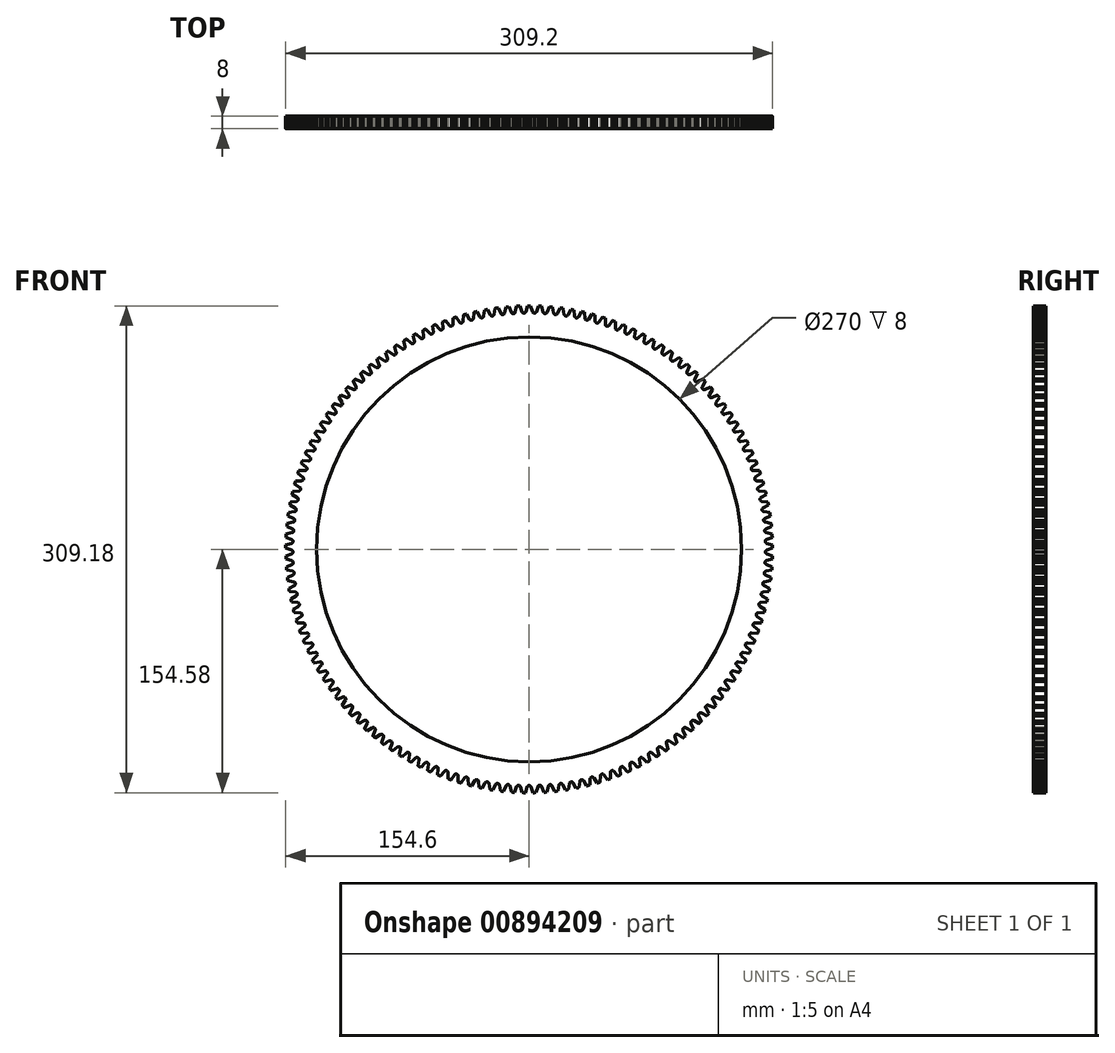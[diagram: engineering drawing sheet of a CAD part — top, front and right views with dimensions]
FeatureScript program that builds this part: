
annotation { "Feature Type Name" : "Feature", "Feature Type Description" : "" }
export const myFeature = defineFeature(function(context is Context, id is Id, definition is map)
    precondition{}
    {
        {
            var Q0;
            Q0=qCreatedBy(makeId("Front.planeOp"),FACE);
            var sketch = newSketch(context, id + "F0", { "sketchPlane" : qUnion([Q0])});
            skCircle(sketch, "E0", {"center": v(0, 0) * mm, "radius": 135 * mm});
            skArc(sketch, "E1", {"start": v(1, 154.6) * mm, "mid": v(0, 154.6) * mm, "end": v(-1, 154.6) * mm});
            skArc(sketch, "E2", {"start": v(2.15, 150.9) * mm, "mid": v(2.6, 150.27) * mm, "end": v(3.34, 150.03) * mm});
            skLineSegment(sketch, "E3", {"start": v(1, 154.6) * mm, "end": v(2.15, 150.9) * mm});
            skArc(sketch, "E4", {"start": v(-3.34, 150.03) * mm, "mid": v(-2.6, 150.27) * mm, "end": v(-2.15, 150.9) * mm});
            skLineSegment(sketch, "E5", {"start": v(-1, 154.6) * mm, "end": v(-2.15, 150.9) * mm});
            skArc(sketch, "E6", {"start": v(-5.89, 154.49) * mm, "mid": v(-6.89, 154.45) * mm, "end": v(-7.89, 154.4) * mm});
            skArc(sketch, "E7", {"start": v(-4.57, 150.85) * mm, "mid": v(-4.1, 150.24) * mm, "end": v(-3.34, 150.03) * mm});
            skLineSegment(sketch, "E8", {"start": v(-5.89, 154.49) * mm, "end": v(-4.57, 150.85) * mm});
            skArc(sketch, "E9", {"start": v(-10.02, 149.73) * mm, "mid": v(-9.3, 150) * mm, "end": v(-8.87, 150.66) * mm});
            skLineSegment(sketch, "E10", {"start": v(-7.89, 154.4) * mm, "end": v(-8.87, 150.66) * mm});
            skArc(sketch, "E11", {"start": v(-12.76, 154.07) * mm, "mid": v(-13.76, 153.99) * mm, "end": v(-14.76, 153.9) * mm});
            skArc(sketch, "E12", {"start": v(-11.3, 150.5) * mm, "mid": v(-10.78, 149.9) * mm, "end": v(-10.02, 149.73) * mm});
            skLineSegment(sketch, "E13", {"start": v(-12.76, 154.07) * mm, "end": v(-11.3, 150.5) * mm});
            skArc(sketch, "E14", {"start": v(-16.68, 149.13) * mm, "mid": v(-15.97, 149.44) * mm, "end": v(-15.57, 150.11) * mm});
            skLineSegment(sketch, "E15", {"start": v(-14.76, 153.9) * mm, "end": v(-15.57, 150.11) * mm});
            skArc(sketch, "E16", {"start": v(-19.61, 153.35) * mm, "mid": v(-20.6, 153.22) * mm, "end": v(-21.6, 153.08) * mm});
            skArc(sketch, "E17", {"start": v(-17.98, 149.84) * mm, "mid": v(-17.45, 149.27) * mm, "end": v(-16.68, 149.13) * mm});
            skLineSegment(sketch, "E18", {"start": v(-19.61, 153.35) * mm, "end": v(-17.98, 149.84) * mm});
            skArc(sketch, "E19", {"start": v(-23.3, 148.24) * mm, "mid": v(-22.6, 148.58) * mm, "end": v(-22.24, 149.27) * mm});
            skLineSegment(sketch, "E20", {"start": v(-21.6, 153.08) * mm, "end": v(-22.24, 149.27) * mm});
            skArc(sketch, "E21", {"start": v(-26.43, 152.32) * mm, "mid": v(-27.41, 152.15) * mm, "end": v(-28.4, 151.97) * mm});
            skArc(sketch, "E22", {"start": v(-24.64, 148.9) * mm, "mid": v(-24.08, 148.35) * mm, "end": v(-23.3, 148.24) * mm});
            skLineSegment(sketch, "E23", {"start": v(-26.43, 152.32) * mm, "end": v(-24.64, 148.9) * mm});
            skArc(sketch, "E24", {"start": v(-29.9, 147.06) * mm, "mid": v(-29.2, 147.43) * mm, "end": v(-28.87, 148.13) * mm});
            skLineSegment(sketch, "E25", {"start": v(-28.4, 151.97) * mm, "end": v(-28.87, 148.13) * mm});
            skArc(sketch, "E26", {"start": v(-33.18, 151) * mm, "mid": v(-34.16, 150.78) * mm, "end": v(-35.14, 150.55) * mm});
            skArc(sketch, "E27", {"start": v(-31.25, 147.65) * mm, "mid": v(-30.67, 147.13) * mm, "end": v(-29.9, 147.06) * mm});
            skLineSegment(sketch, "E28", {"start": v(-33.18, 151) * mm, "end": v(-31.25, 147.65) * mm});
            skArc(sketch, "E29", {"start": v(-36.41, 145.58) * mm, "mid": v(-35.74, 145.98) * mm, "end": v(-35.44, 146.7) * mm});
            skLineSegment(sketch, "E30", {"start": v(-35.14, 150.55) * mm, "end": v(-35.44, 146.7) * mm});
            skArc(sketch, "E31", {"start": v(-39.88, 149.37) * mm, "mid": v(-40.84, 149.1) * mm, "end": v(-41.8, 148.84) * mm});
            skArc(sketch, "E32", {"start": v(-37.8, 146.11) * mm, "mid": v(-37.2, 145.62) * mm, "end": v(-36.41, 145.58) * mm});
            skLineSegment(sketch, "E33", {"start": v(-39.88, 149.37) * mm, "end": v(-37.8, 146.11) * mm});
            skArc(sketch, "E34", {"start": v(-42.86, 143.81) * mm, "mid": v(-42.21, 144.24) * mm, "end": v(-41.94, 144.97) * mm});
            skLineSegment(sketch, "E35", {"start": v(-41.8, 148.84) * mm, "end": v(-41.94, 144.97) * mm});
            skArc(sketch, "E36", {"start": v(-46.5, 147.44) * mm, "mid": v(-47.45, 147.14) * mm, "end": v(-48.4, 146.83) * mm});
            skArc(sketch, "E37", {"start": v(-44.27, 144.28) * mm, "mid": v(-43.64, 143.82) * mm, "end": v(-42.86, 143.81) * mm});
            skLineSegment(sketch, "E38", {"start": v(-46.5, 147.44) * mm, "end": v(-44.27, 144.28) * mm});
            skArc(sketch, "E39", {"start": v(-49.22, 141.76) * mm, "mid": v(-48.6, 142.22) * mm, "end": v(-48.36, 142.96) * mm});
            skLineSegment(sketch, "E40", {"start": v(-48.4, 146.83) * mm, "end": v(-48.36, 142.96) * mm});
            skArc(sketch, "E41", {"start": v(-53.01, 145.23) * mm, "mid": v(-53.95, 144.88) * mm, "end": v(-54.9, 144.53) * mm});
            skArc(sketch, "E42", {"start": v(-50.65, 142.17) * mm, "mid": v(-50, 141.73) * mm, "end": v(-49.22, 141.76) * mm});
            skLineSegment(sketch, "E43", {"start": v(-53.01, 145.23) * mm, "end": v(-50.65, 142.17) * mm});
            skArc(sketch, "E44", {"start": v(-55.5, 139.43) * mm, "mid": v(-54.88, 139.91) * mm, "end": v(-54.68, 140.67) * mm});
            skLineSegment(sketch, "E45", {"start": v(-54.9, 144.53) * mm, "end": v(-54.68, 140.67) * mm});
            skArc(sketch, "E46", {"start": v(-59.43, 142.72) * mm, "mid": v(-60.35, 142.33) * mm, "end": v(-61.27, 141.94) * mm});
            skArc(sketch, "E47", {"start": v(-56.93, 139.77) * mm, "mid": v(-56.27, 139.36) * mm, "end": v(-55.5, 139.43) * mm});
            skLineSegment(sketch, "E48", {"start": v(-59.43, 142.72) * mm, "end": v(-56.93, 139.77) * mm});
            skArc(sketch, "E49", {"start": v(-61.65, 136.82) * mm, "mid": v(-61.06, 137.33) * mm, "end": v(-60.9, 138.1) * mm});
            skLineSegment(sketch, "E50", {"start": v(-61.27, 141.94) * mm, "end": v(-60.9, 138.1) * mm});
            skArc(sketch, "E51", {"start": v(-65.73, 139.93) * mm, "mid": v(-66.63, 139.5) * mm, "end": v(-67.54, 139.07) * mm});
            skArc(sketch, "E52", {"start": v(-63.1, 137.1) * mm, "mid": v(-62.42, 136.72) * mm, "end": v(-61.65, 136.82) * mm});
            skLineSegment(sketch, "E53", {"start": v(-65.73, 139.93) * mm, "end": v(-63.1, 137.1) * mm});
            skArc(sketch, "E54", {"start": v(-67.68, 133.93) * mm, "mid": v(-67.12, 134.47) * mm, "end": v(-66.98, 135.24) * mm});
            skLineSegment(sketch, "E55", {"start": v(-67.54, 139.07) * mm, "end": v(-66.98, 135.24) * mm});
            skArc(sketch, "E56", {"start": v(-71.9, 136.86) * mm, "mid": v(-72.78, 136.4) * mm, "end": v(-73.66, 135.92) * mm});
            skArc(sketch, "E57", {"start": v(-69.15, 134.15) * mm, "mid": v(-68.45, 133.8) * mm, "end": v(-67.68, 133.93) * mm});
            skLineSegment(sketch, "E58", {"start": v(-71.9, 136.86) * mm, "end": v(-69.15, 134.15) * mm});
            skArc(sketch, "E59", {"start": v(-73.58, 130.79) * mm, "mid": v(-73.04, 131.35) * mm, "end": v(-72.94, 132.12) * mm});
            skLineSegment(sketch, "E60", {"start": v(-73.66, 135.92) * mm, "end": v(-72.94, 132.12) * mm});
            skArc(sketch, "E61", {"start": v(-77.92, 133.53) * mm, "mid": v(-78.79, 133.02) * mm, "end": v(-79.65, 132.5) * mm});
            skArc(sketch, "E62", {"start": v(-75.05, 130.93) * mm, "mid": v(-74.34, 130.62) * mm, "end": v(-73.58, 130.79) * mm});
            skLineSegment(sketch, "E63", {"start": v(-77.92, 133.53) * mm, "end": v(-75.05, 130.93) * mm});
            skArc(sketch, "E64", {"start": v(-79.33, 127.38) * mm, "mid": v(-78.82, 127.97) * mm, "end": v(-78.75, 128.74) * mm});
            skLineSegment(sketch, "E65", {"start": v(-79.65, 132.5) * mm, "end": v(-78.75, 128.74) * mm});
            skArc(sketch, "E66", {"start": v(-83.8, 129.92) * mm, "mid": v(-84.63, 129.38) * mm, "end": v(-85.47, 128.83) * mm});
            skArc(sketch, "E67", {"start": v(-80.81, 127.46) * mm, "mid": v(-80.09, 127.18) * mm, "end": v(-79.33, 127.38) * mm});
            skLineSegment(sketch, "E68", {"start": v(-83.8, 129.92) * mm, "end": v(-80.81, 127.46) * mm});
            skArc(sketch, "E69", {"start": v(-84.93, 123.72) * mm, "mid": v(-84.44, 124.33) * mm, "end": v(-84.4, 125.1) * mm});
            skLineSegment(sketch, "E70", {"start": v(-85.47, 128.83) * mm, "end": v(-84.4, 125.1) * mm});
            skArc(sketch, "E71", {"start": v(-89.5, 126.06) * mm, "mid": v(-90.31, 125.48) * mm, "end": v(-91.12, 124.9) * mm});
            skArc(sketch, "E72", {"start": v(-86.4, 123.73) * mm, "mid": v(-85.67, 123.48) * mm, "end": v(-84.93, 123.72) * mm});
            skLineSegment(sketch, "E73", {"start": v(-89.5, 126.06) * mm, "end": v(-86.4, 123.73) * mm});
            skArc(sketch, "E74", {"start": v(-90.35, 119.81) * mm, "mid": v(-89.9, 120.44) * mm, "end": v(-89.9, 121.22) * mm});
            skLineSegment(sketch, "E75", {"start": v(-91.12, 124.9) * mm, "end": v(-89.9, 121.22) * mm});
            skArc(sketch, "E76", {"start": v(-95.03, 121.95) * mm, "mid": v(-95.81, 121.33) * mm, "end": v(-96.6, 120.7) * mm});
            skArc(sketch, "E77", {"start": v(-91.84, 119.76) * mm, "mid": v(-91.09, 119.54) * mm, "end": v(-90.35, 119.81) * mm});
            skLineSegment(sketch, "E78", {"start": v(-95.03, 121.95) * mm, "end": v(-91.84, 119.76) * mm});
            skArc(sketch, "E79", {"start": v(-95.6, 115.67) * mm, "mid": v(-95.17, 116.32) * mm, "end": v(-95.2, 117.1) * mm});
            skLineSegment(sketch, "E80", {"start": v(-96.6, 120.7) * mm, "end": v(-95.2, 117.1) * mm});
            skArc(sketch, "E81", {"start": v(-100.36, 117.6) * mm, "mid": v(-101.12, 116.94) * mm, "end": v(-101.88, 116.28) * mm});
            skArc(sketch, "E82", {"start": v(-97.08, 115.55) * mm, "mid": v(-96.32, 115.37) * mm, "end": v(-95.6, 115.67) * mm});
            skLineSegment(sketch, "E83", {"start": v(-100.36, 117.6) * mm, "end": v(-97.08, 115.55) * mm});
            skArc(sketch, "E84", {"start": v(-100.66, 111.3) * mm, "mid": v(-100.26, 111.96) * mm, "end": v(-100.33, 112.74) * mm});
            skLineSegment(sketch, "E85", {"start": v(-101.88, 116.28) * mm, "end": v(-100.33, 112.74) * mm});
            skArc(sketch, "E86", {"start": v(-105.5, 113) * mm, "mid": v(-106.23, 112.32) * mm, "end": v(-106.96, 111.63) * mm});
            skArc(sketch, "E87", {"start": v(-102.13, 111.11) * mm, "mid": v(-101.37, 110.96) * mm, "end": v(-100.66, 111.3) * mm});
            skLineSegment(sketch, "E88", {"start": v(-105.5, 113) * mm, "end": v(-102.13, 111.11) * mm});
            skArc(sketch, "E89", {"start": v(-105.52, 106.7) * mm, "mid": v(-105.15, 107.39) * mm, "end": v(-105.25, 108.16) * mm});
            skLineSegment(sketch, "E90", {"start": v(-106.96, 111.63) * mm, "end": v(-105.25, 108.16) * mm});
            skArc(sketch, "E91", {"start": v(-110.43, 108.2) * mm, "mid": v(-111.13, 107.48) * mm, "end": v(-111.82, 106.75) * mm});
            skArc(sketch, "E92", {"start": v(-106.98, 106.45) * mm, "mid": v(-106.2, 106.34) * mm, "end": v(-105.52, 106.7) * mm});
            skLineSegment(sketch, "E93", {"start": v(-110.43, 108.2) * mm, "end": v(-106.98, 106.45) * mm});
            skArc(sketch, "E94", {"start": v(-110.17, 101.9) * mm, "mid": v(-109.83, 102.6) * mm, "end": v(-109.97, 103.36) * mm});
            skLineSegment(sketch, "E95", {"start": v(-111.82, 106.75) * mm, "end": v(-109.97, 103.36) * mm});
            skArc(sketch, "E96", {"start": v(-115.14, 103.17) * mm, "mid": v(-115.8, 102.42) * mm, "end": v(-116.47, 101.67) * mm});
            skArc(sketch, "E97", {"start": v(-111.62, 101.58) * mm, "mid": v(-110.84, 101.5) * mm, "end": v(-110.17, 101.9) * mm});
            skLineSegment(sketch, "E98", {"start": v(-115.14, 103.17) * mm, "end": v(-111.62, 101.58) * mm});
            skArc(sketch, "E99", {"start": v(-114.6, 96.88) * mm, "mid": v(-114.29, 97.6) * mm, "end": v(-114.46, 98.36) * mm});
            skLineSegment(sketch, "E100", {"start": v(-116.47, 101.67) * mm, "end": v(-114.46, 98.36) * mm});
            skArc(sketch, "E101", {"start": v(-119.62, 97.94) * mm, "mid": v(-120.26, 97.16) * mm, "end": v(-120.88, 96.38) * mm});
            skArc(sketch, "E102", {"start": v(-116.03, 96.5) * mm, "mid": v(-115.25, 96.46) * mm, "end": v(-114.6, 96.88) * mm});
            skLineSegment(sketch, "E103", {"start": v(-119.62, 97.94) * mm, "end": v(-116.03, 96.5) * mm});
            skArc(sketch, "E104", {"start": v(-118.8, 91.68) * mm, "mid": v(-118.52, 92.41) * mm, "end": v(-118.73, 93.16) * mm});
            skLineSegment(sketch, "E105", {"start": v(-120.88, 96.38) * mm, "end": v(-118.73, 93.16) * mm});
            skArc(sketch, "E106", {"start": v(-123.87, 92.5) * mm, "mid": v(-124.46, 91.7) * mm, "end": v(-125.05, 90.9) * mm});
            skArc(sketch, "E107", {"start": v(-120.21, 91.24) * mm, "mid": v(-119.43, 91.23) * mm, "end": v(-118.8, 91.68) * mm});
            skLineSegment(sketch, "E108", {"start": v(-123.87, 92.5) * mm, "end": v(-120.21, 91.24) * mm});
            skArc(sketch, "E109", {"start": v(-122.76, 86.3) * mm, "mid": v(-122.52, 87.04) * mm, "end": v(-122.76, 87.78) * mm});
            skLineSegment(sketch, "E110", {"start": v(-125.05, 90.9) * mm, "end": v(-122.76, 87.78) * mm});
            skArc(sketch, "E111", {"start": v(-127.87, 86.9) * mm, "mid": v(-128.43, 86.07) * mm, "end": v(-128.98, 85.24) * mm});
            skArc(sketch, "E112", {"start": v(-124.16, 85.8) * mm, "mid": v(-123.38, 85.82) * mm, "end": v(-122.76, 86.3) * mm});
            skLineSegment(sketch, "E113", {"start": v(-127.87, 86.9) * mm, "end": v(-124.16, 85.8) * mm});
            skArc(sketch, "E114", {"start": v(-126.49, 80.75) * mm, "mid": v(-126.28, 81.5) * mm, "end": v(-126.55, 82.23) * mm});
            skLineSegment(sketch, "E115", {"start": v(-128.98, 85.24) * mm, "end": v(-126.55, 82.23) * mm});
            skArc(sketch, "E116", {"start": v(-131.6, 81.12) * mm, "mid": v(-132.13, 80.26) * mm, "end": v(-132.65, 79.4) * mm});
            skArc(sketch, "E117", {"start": v(-127.86, 80.18) * mm, "mid": v(-127.08, 80.24) * mm, "end": v(-126.49, 80.75) * mm});
            skLineSegment(sketch, "E118", {"start": v(-131.6, 81.12) * mm, "end": v(-127.86, 80.18) * mm});
            skArc(sketch, "E119", {"start": v(-129.96, 75.03) * mm, "mid": v(-129.78, 75.8) * mm, "end": v(-130.09, 76.5) * mm});
            skLineSegment(sketch, "E120", {"start": v(-132.65, 79.4) * mm, "end": v(-130.09, 76.5) * mm});
            skArc(sketch, "E121", {"start": v(-135.1, 75.17) * mm, "mid": v(-135.58, 74.3) * mm, "end": v(-136.05, 73.42) * mm});
            skArc(sketch, "E122", {"start": v(-131.3, 74.4) * mm, "mid": v(-130.53, 74.5) * mm, "end": v(-129.96, 75.03) * mm});
            skLineSegment(sketch, "E123", {"start": v(-135.1, 75.17) * mm, "end": v(-131.3, 74.4) * mm});
            skArc(sketch, "E124", {"start": v(-133.17, 69.17) * mm, "mid": v(-133.03, 69.93) * mm, "end": v(-133.37, 70.64) * mm});
            skLineSegment(sketch, "E125", {"start": v(-136.05, 73.42) * mm, "end": v(-133.37, 70.64) * mm});
            skArc(sketch, "E126", {"start": v(-138.3, 69.08) * mm, "mid": v(-138.75, 68.18) * mm, "end": v(-139.2, 67.28) * mm});
            skArc(sketch, "E127", {"start": v(-134.49, 68.48) * mm, "mid": v(-133.72, 68.6) * mm, "end": v(-133.17, 69.17) * mm});
            skLineSegment(sketch, "E128", {"start": v(-138.3, 69.08) * mm, "end": v(-134.49, 68.48) * mm});
            skArc(sketch, "E129", {"start": v(-136.12, 63.17) * mm, "mid": v(-136.01, 63.94) * mm, "end": v(-136.38, 64.63) * mm});
            skLineSegment(sketch, "E130", {"start": v(-139.2, 67.28) * mm, "end": v(-136.38, 64.63) * mm});
            skArc(sketch, "E131", {"start": v(-141.25, 62.85) * mm, "mid": v(-141.65, 61.94) * mm, "end": v(-142.05, 61.02) * mm});
            skArc(sketch, "E132", {"start": v(-137.4, 62.43) * mm, "mid": v(-136.64, 62.59) * mm, "end": v(-136.12, 63.17) * mm});
            skLineSegment(sketch, "E133", {"start": v(-141.25, 62.85) * mm, "end": v(-137.4, 62.43) * mm});
            skArc(sketch, "E134", {"start": v(-138.8, 57.04) * mm, "mid": v(-138.73, 57.82) * mm, "end": v(-139.13, 58.49) * mm});
            skLineSegment(sketch, "E135", {"start": v(-142.05, 61.02) * mm, "end": v(-139.13, 58.49) * mm});
            skArc(sketch, "E136", {"start": v(-143.9, 56.5) * mm, "mid": v(-144.27, 55.56) * mm, "end": v(-144.63, 54.63) * mm});
            skArc(sketch, "E137", {"start": v(-140.05, 56.24) * mm, "mid": v(-139.3, 56.44) * mm, "end": v(-138.8, 57.04) * mm});
            skLineSegment(sketch, "E138", {"start": v(-143.9, 56.5) * mm, "end": v(-140.05, 56.24) * mm});
            skArc(sketch, "E139", {"start": v(-141.2, 50.8) * mm, "mid": v(-141.16, 51.58) * mm, "end": v(-141.6, 52.23) * mm});
            skLineSegment(sketch, "E140", {"start": v(-144.63, 54.63) * mm, "end": v(-141.6, 52.23) * mm});
            skArc(sketch, "E141", {"start": v(-146.28, 50.03) * mm, "mid": v(-146.6, 49.08) * mm, "end": v(-146.92, 48.13) * mm});
            skArc(sketch, "E142", {"start": v(-142.41, 49.95) * mm, "mid": v(-141.67, 50.18) * mm, "end": v(-141.2, 50.8) * mm});
            skLineSegment(sketch, "E143", {"start": v(-146.28, 50.03) * mm, "end": v(-142.41, 49.95) * mm});
            skArc(sketch, "E144", {"start": v(-143.33, 44.46) * mm, "mid": v(-143.32, 45.24) * mm, "end": v(-143.78, 45.87) * mm});
            skLineSegment(sketch, "E145", {"start": v(-146.92, 48.13) * mm, "end": v(-143.78, 45.87) * mm});
            skArc(sketch, "E146", {"start": v(-148.36, 43.46) * mm, "mid": v(-148.64, 42.5) * mm, "end": v(-148.91, 41.54) * mm});
            skArc(sketch, "E147", {"start": v(-144.5, 43.55) * mm, "mid": v(-143.76, 43.81) * mm, "end": v(-143.33, 44.46) * mm});
            skLineSegment(sketch, "E148", {"start": v(-148.36, 43.46) * mm, "end": v(-144.5, 43.55) * mm});
            skArc(sketch, "E149", {"start": v(-145.16, 38.03) * mm, "mid": v(-145.2, 38.81) * mm, "end": v(-145.68, 39.42) * mm});
            skLineSegment(sketch, "E150", {"start": v(-148.91, 41.54) * mm, "end": v(-145.68, 39.42) * mm});
            skArc(sketch, "E151", {"start": v(-150.15, 36.81) * mm, "mid": v(-150.39, 35.84) * mm, "end": v(-150.62, 34.86) * mm});
            skArc(sketch, "E152", {"start": v(-146.3, 37.07) * mm, "mid": v(-145.57, 37.37) * mm, "end": v(-145.16, 38.03) * mm});
            skLineSegment(sketch, "E153", {"start": v(-150.15, 36.81) * mm, "end": v(-146.3, 37.07) * mm});
            skArc(sketch, "E154", {"start": v(-146.71, 31.53) * mm, "mid": v(-146.78, 32.3) * mm, "end": v(-147.3, 32.9) * mm});
            skLineSegment(sketch, "E155", {"start": v(-150.62, 34.86) * mm, "end": v(-147.3, 32.9) * mm});
            skArc(sketch, "E156", {"start": v(-151.64, 30.09) * mm, "mid": v(-151.84, 29.1) * mm, "end": v(-152.02, 28.12) * mm});
            skArc(sketch, "E157", {"start": v(-147.8, 30.52) * mm, "mid": v(-147.1, 30.84) * mm, "end": v(-146.71, 31.53) * mm});
            skLineSegment(sketch, "E158", {"start": v(-151.64, 30.09) * mm, "end": v(-147.8, 30.52) * mm});
            skArc(sketch, "E159", {"start": v(-147.97, 24.96) * mm, "mid": v(-148.07, 25.73) * mm, "end": v(-148.61, 26.3) * mm});
            skLineSegment(sketch, "E160", {"start": v(-152.02, 28.12) * mm, "end": v(-148.61, 26.3) * mm});
            skArc(sketch, "E161", {"start": v(-152.83, 23.3) * mm, "mid": v(-152.98, 22.31) * mm, "end": v(-153.12, 21.32) * mm});
            skArc(sketch, "E162", {"start": v(-149.01, 23.9) * mm, "mid": v(-148.32, 24.26) * mm, "end": v(-147.97, 24.96) * mm});
            skLineSegment(sketch, "E163", {"start": v(-152.83, 23.3) * mm, "end": v(-149.01, 23.9) * mm});
            skArc(sketch, "E164", {"start": v(-148.94, 18.34) * mm, "mid": v(-149.07, 19.11) * mm, "end": v(-149.63, 19.65) * mm});
            skLineSegment(sketch, "E165", {"start": v(-153.12, 21.32) * mm, "end": v(-149.63, 19.65) * mm});
            skArc(sketch, "E166", {"start": v(-153.72, 16.47) * mm, "mid": v(-153.82, 15.47) * mm, "end": v(-153.92, 14.48) * mm});
            skArc(sketch, "E167", {"start": v(-149.93, 17.24) * mm, "mid": v(-149.25, 17.63) * mm, "end": v(-148.94, 18.34) * mm});
            skLineSegment(sketch, "E168", {"start": v(-153.72, 16.47) * mm, "end": v(-149.93, 17.24) * mm});
            skArc(sketch, "E169", {"start": v(-149.6, 11.7) * mm, "mid": v(-149.77, 12.45) * mm, "end": v(-150.36, 12.97) * mm});
            skLineSegment(sketch, "E170", {"start": v(-153.92, 14.48) * mm, "end": v(-150.36, 12.97) * mm});
            skArc(sketch, "E171", {"start": v(-154.3, 9.6) * mm, "mid": v(-154.36, 8.6) * mm, "end": v(-154.41, 7.6) * mm});
            skArc(sketch, "E172", {"start": v(-150.55, 10.55) * mm, "mid": v(-149.9, 10.96) * mm, "end": v(-149.6, 11.7) * mm});
            skLineSegment(sketch, "E173", {"start": v(-154.3, 9.6) * mm, "end": v(-150.55, 10.55) * mm});
            skArc(sketch, "E174", {"start": v(-149.98, 5.01) * mm, "mid": v(-150.18, 5.77) * mm, "end": v(-150.79, 6.25) * mm});
            skLineSegment(sketch, "E175", {"start": v(-154.41, 7.6) * mm, "end": v(-150.79, 6.25) * mm});
            skArc(sketch, "E176", {"start": v(-154.58, 2.72) * mm, "mid": v(-154.6, 1.72) * mm, "end": v(-154.6, 0.72) * mm});
            skArc(sketch, "E177", {"start": v(-150.87, 3.83) * mm, "mid": v(-150.23, 4.28) * mm, "end": v(-149.98, 5.01) * mm});
            skLineSegment(sketch, "E178", {"start": v(-154.58, 2.72) * mm, "end": v(-150.87, 3.83) * mm});
            skArc(sketch, "E179", {"start": v(-150.05, -1.67) * mm, "mid": v(-150.29, -0.93) * mm, "end": v(-150.92, -0.47) * mm});
            skLineSegment(sketch, "E180", {"start": v(-154.6, 0.72) * mm, "end": v(-150.92, -0.47) * mm});
            skArc(sketch, "E181", {"start": v(-154.54, -4.17) * mm, "mid": v(-154.51, -5.17) * mm, "end": v(-154.48, -6.17) * mm});
            skArc(sketch, "E182", {"start": v(-150.9, -2.9) * mm, "mid": v(-150.27, -2.42) * mm, "end": v(-150.05, -1.67) * mm});
            skLineSegment(sketch, "E183", {"start": v(-154.54, -4.17) * mm, "end": v(-150.9, -2.9) * mm});
            skArc(sketch, "E184", {"start": v(-149.83, -8.35) * mm, "mid": v(-150.1, -7.62) * mm, "end": v(-150.75, -7.2) * mm});
            skLineSegment(sketch, "E185", {"start": v(-154.48, -6.17) * mm, "end": v(-150.75, -7.2) * mm});
            skArc(sketch, "E186", {"start": v(-154.2, -11.05) * mm, "mid": v(-154.13, -12.04) * mm, "end": v(-154.05, -13.04) * mm});
            skArc(sketch, "E187", {"start": v(-150.61, -9.61) * mm, "mid": v(-150.01, -9.11) * mm, "end": v(-149.83, -8.35) * mm});
            skLineSegment(sketch, "E188", {"start": v(-154.2, -11.05) * mm, "end": v(-150.61, -9.61) * mm});
            skArc(sketch, "E189", {"start": v(-149.3, -15.02) * mm, "mid": v(-149.6, -14.3) * mm, "end": v(-150.28, -13.9) * mm});
            skLineSegment(sketch, "E190", {"start": v(-154.05, -13.04) * mm, "end": v(-150.28, -13.9) * mm});
            skArc(sketch, "E191", {"start": v(-153.56, -17.9) * mm, "mid": v(-153.44, -18.9) * mm, "end": v(-153.32, -19.9) * mm});
            skArc(sketch, "E192", {"start": v(-150.04, -16.31) * mm, "mid": v(-149.46, -15.79) * mm, "end": v(-149.3, -15.02) * mm});
            skLineSegment(sketch, "E193", {"start": v(-153.56, -17.9) * mm, "end": v(-150.04, -16.31) * mm});
            skArc(sketch, "E194", {"start": v(-148.5, -21.66) * mm, "mid": v(-148.82, -20.95) * mm, "end": v(-149.5, -20.58) * mm});
            skLineSegment(sketch, "E195", {"start": v(-153.32, -19.9) * mm, "end": v(-149.5, -20.58) * mm});
            skArc(sketch, "E196", {"start": v(-152.6, -24.73) * mm, "mid": v(-152.45, -25.71) * mm, "end": v(-152.28, -26.7) * mm});
            skArc(sketch, "E197", {"start": v(-149.16, -22.98) * mm, "mid": v(-148.6, -22.43) * mm, "end": v(-148.5, -21.66) * mm});
            skLineSegment(sketch, "E198", {"start": v(-152.6, -24.73) * mm, "end": v(-149.16, -22.98) * mm});
            skArc(sketch, "E199", {"start": v(-147.38, -28.25) * mm, "mid": v(-147.74, -27.56) * mm, "end": v(-148.44, -27.22) * mm});
            skLineSegment(sketch, "E200", {"start": v(-152.28, -26.7) * mm, "end": v(-148.44, -27.22) * mm});
            skArc(sketch, "E201", {"start": v(-151.36, -31.5) * mm, "mid": v(-151.15, -32.48) * mm, "end": v(-150.94, -33.46) * mm});
            skArc(sketch, "E202", {"start": v(-147.99, -29.6) * mm, "mid": v(-147.46, -29.03) * mm, "end": v(-147.38, -28.25) * mm});
            skLineSegment(sketch, "E203", {"start": v(-151.36, -31.5) * mm, "end": v(-147.99, -29.6) * mm});
            skArc(sketch, "E204", {"start": v(-145.97, -34.79) * mm, "mid": v(-146.37, -34.11) * mm, "end": v(-147.08, -33.8) * mm});
            skLineSegment(sketch, "E205", {"start": v(-150.94, -33.46) * mm, "end": v(-147.08, -33.8) * mm});
            skArc(sketch, "E206", {"start": v(-149.8, -38.21) * mm, "mid": v(-149.55, -39.18) * mm, "end": v(-149.3, -40.15) * mm});
            skArc(sketch, "E207", {"start": v(-146.52, -36.16) * mm, "mid": v(-146.02, -35.57) * mm, "end": v(-145.97, -34.79) * mm});
            skLineSegment(sketch, "E208", {"start": v(-149.8, -38.21) * mm, "end": v(-146.52, -36.16) * mm});
            skArc(sketch, "E209", {"start": v(-144.28, -41.26) * mm, "mid": v(-144.7, -40.6) * mm, "end": v(-145.43, -40.32) * mm});
            skLineSegment(sketch, "E210", {"start": v(-149.3, -40.15) * mm, "end": v(-145.43, -40.32) * mm});
            skArc(sketch, "E211", {"start": v(-147.95, -44.85) * mm, "mid": v(-147.66, -45.8) * mm, "end": v(-147.36, -46.76) * mm});
            skArc(sketch, "E212", {"start": v(-144.77, -42.66) * mm, "mid": v(-144.3, -42.04) * mm, "end": v(-144.28, -41.26) * mm});
            skLineSegment(sketch, "E213", {"start": v(-147.95, -44.85) * mm, "end": v(-144.77, -42.66) * mm});
            skArc(sketch, "E214", {"start": v(-142.3, -47.64) * mm, "mid": v(-142.75, -47) * mm, "end": v(-143.5, -46.76) * mm});
            skLineSegment(sketch, "E215", {"start": v(-147.36, -46.76) * mm, "end": v(-143.5, -46.76) * mm});
            skArc(sketch, "E216", {"start": v(-145.8, -51.4) * mm, "mid": v(-145.47, -52.34) * mm, "end": v(-145.13, -53.28) * mm});
            skArc(sketch, "E217", {"start": v(-142.72, -49.06) * mm, "mid": v(-142.28, -48.42) * mm, "end": v(-142.3, -47.64) * mm});
            skLineSegment(sketch, "E218", {"start": v(-145.8, -51.4) * mm, "end": v(-142.72, -49.06) * mm});
            skArc(sketch, "E219", {"start": v(-140.04, -53.93) * mm, "mid": v(-140.52, -53.32) * mm, "end": v(-141.27, -53.1) * mm});
            skLineSegment(sketch, "E220", {"start": v(-145.13, -53.28) * mm, "end": v(-141.27, -53.1) * mm});
            skArc(sketch, "E221", {"start": v(-143.37, -57.84) * mm, "mid": v(-143, -58.76) * mm, "end": v(-142.61, -59.69) * mm});
            skArc(sketch, "E222", {"start": v(-140.4, -55.37) * mm, "mid": v(-139.98, -54.71) * mm, "end": v(-140.04, -53.93) * mm});
            skLineSegment(sketch, "E223", {"start": v(-143.37, -57.84) * mm, "end": v(-140.4, -55.37) * mm});
            skArc(sketch, "E224", {"start": v(-137.5, -60.12) * mm, "mid": v(-138, -59.53) * mm, "end": v(-138.76, -59.35) * mm});
            skLineSegment(sketch, "E225", {"start": v(-142.61, -59.69) * mm, "end": v(-138.76, -59.35) * mm});
            skArc(sketch, "E226", {"start": v(-140.65, -64.17) * mm, "mid": v(-140.24, -65.08) * mm, "end": v(-139.81, -65.98) * mm});
            skArc(sketch, "E227", {"start": v(-137.79, -61.57) * mm, "mid": v(-137.4, -60.9) * mm, "end": v(-137.5, -60.12) * mm});
            skLineSegment(sketch, "E228", {"start": v(-140.65, -64.17) * mm, "end": v(-137.79, -61.57) * mm});
            skArc(sketch, "E229", {"start": v(-134.68, -66.18) * mm, "mid": v(-135.21, -65.61) * mm, "end": v(-135.98, -65.47) * mm});
            skLineSegment(sketch, "E230", {"start": v(-139.81, -65.98) * mm, "end": v(-135.98, -65.47) * mm});
            skArc(sketch, "E231", {"start": v(-137.66, -70.37) * mm, "mid": v(-137.2, -71.26) * mm, "end": v(-136.73, -72.15) * mm});
            skArc(sketch, "E232", {"start": v(-134.9, -67.65) * mm, "mid": v(-134.55, -66.95) * mm, "end": v(-134.68, -66.18) * mm});
            skLineSegment(sketch, "E233", {"start": v(-137.66, -70.37) * mm, "end": v(-134.9, -67.65) * mm});
            skArc(sketch, "E234", {"start": v(-131.6, -72.12) * mm, "mid": v(-132.16, -71.57) * mm, "end": v(-132.93, -71.46) * mm});
            skLineSegment(sketch, "E235", {"start": v(-136.73, -72.15) * mm, "end": v(-132.93, -71.46) * mm});
            skArc(sketch, "E236", {"start": v(-134.39, -76.43) * mm, "mid": v(-133.89, -77.3) * mm, "end": v(-133.38, -78.17) * mm});
            skArc(sketch, "E237", {"start": v(-131.76, -73.6) * mm, "mid": v(-131.44, -72.88) * mm, "end": v(-131.6, -72.12) * mm});
            skLineSegment(sketch, "E238", {"start": v(-134.39, -76.43) * mm, "end": v(-131.76, -73.6) * mm});
            skArc(sketch, "E239", {"start": v(-128.25, -77.9) * mm, "mid": v(-128.84, -77.39) * mm, "end": v(-129.61, -77.31) * mm});
            skLineSegment(sketch, "E240", {"start": v(-133.38, -78.17) * mm, "end": v(-129.61, -77.31) * mm});
            skArc(sketch, "E241", {"start": v(-130.85, -82.34) * mm, "mid": v(-130.31, -83.19) * mm, "end": v(-129.77, -84.03) * mm});
            skArc(sketch, "E242", {"start": v(-128.35, -79.39) * mm, "mid": v(-128.06, -78.66) * mm, "end": v(-128.25, -77.9) * mm});
            skLineSegment(sketch, "E243", {"start": v(-130.85, -82.34) * mm, "end": v(-128.35, -79.39) * mm});
            skArc(sketch, "E244", {"start": v(-124.66, -83.54) * mm, "mid": v(-125.26, -83.05) * mm, "end": v(-126.04, -83.01) * mm});
            skLineSegment(sketch, "E245", {"start": v(-129.77, -84.03) * mm, "end": v(-126.04, -83.01) * mm});
            skArc(sketch, "E246", {"start": v(-127.05, -88.09) * mm, "mid": v(-126.48, -88.9) * mm, "end": v(-125.9, -89.73) * mm});
            skArc(sketch, "E247", {"start": v(-124.69, -85.03) * mm, "mid": v(-124.43, -84.3) * mm, "end": v(-124.66, -83.54) * mm});
            skLineSegment(sketch, "E248", {"start": v(-127.05, -88.09) * mm, "end": v(-124.69, -85.03) * mm});
            skArc(sketch, "E249", {"start": v(-120.81, -89.01) * mm, "mid": v(-121.44, -88.55) * mm, "end": v(-122.22, -88.54) * mm});
            skLineSegment(sketch, "E250", {"start": v(-125.9, -89.73) * mm, "end": v(-122.22, -88.54) * mm});
            skArc(sketch, "E251", {"start": v(-123, -93.66) * mm, "mid": v(-122.39, -94.46) * mm, "end": v(-121.78, -95.25) * mm});
            skArc(sketch, "E252", {"start": v(-120.78, -90.5) * mm, "mid": v(-120.55, -89.75) * mm, "end": v(-120.81, -89.01) * mm});
            skLineSegment(sketch, "E253", {"start": v(-123, -93.66) * mm, "end": v(-120.78, -90.5) * mm});
            skArc(sketch, "E254", {"start": v(-116.73, -94.3) * mm, "mid": v(-117.37, -93.87) * mm, "end": v(-118.15, -93.9) * mm});
            skLineSegment(sketch, "E255", {"start": v(-121.78, -95.25) * mm, "end": v(-118.15, -93.9) * mm});
            skArc(sketch, "E256", {"start": v(-118.7, -99.05) * mm, "mid": v(-118.06, -99.81) * mm, "end": v(-117.41, -100.58) * mm});
            skArc(sketch, "E257", {"start": v(-116.63, -95.79) * mm, "mid": v(-116.43, -95.03) * mm, "end": v(-116.73, -94.3) * mm});
            skLineSegment(sketch, "E258", {"start": v(-118.7, -99.05) * mm, "end": v(-116.63, -95.79) * mm});
            skArc(sketch, "E259", {"start": v(-112.4, -99.41) * mm, "mid": v(-113.07, -99) * mm, "end": v(-113.85, -99.07) * mm});
            skLineSegment(sketch, "E260", {"start": v(-117.41, -100.58) * mm, "end": v(-113.85, -99.07) * mm});
            skArc(sketch, "E261", {"start": v(-114.17, -104.24) * mm, "mid": v(-113.5, -104.97) * mm, "end": v(-112.81, -105.7) * mm});
            skArc(sketch, "E262", {"start": v(-112.24, -100.89) * mm, "mid": v(-112.08, -100.12) * mm, "end": v(-112.4, -99.41) * mm});
            skLineSegment(sketch, "E263", {"start": v(-114.17, -104.24) * mm, "end": v(-112.24, -100.89) * mm});
            skArc(sketch, "E264", {"start": v(-107.87, -104.32) * mm, "mid": v(-108.55, -103.94) * mm, "end": v(-109.32, -104.04) * mm});
            skLineSegment(sketch, "E265", {"start": v(-112.81, -105.7) * mm, "end": v(-109.32, -104.04) * mm});
            skArc(sketch, "E266", {"start": v(-109.42, -109.22) * mm, "mid": v(-108.7, -109.93) * mm, "end": v(-108, -110.63) * mm});
            skArc(sketch, "E267", {"start": v(-107.64, -105.79) * mm, "mid": v(-107.51, -105.02) * mm, "end": v(-107.87, -104.32) * mm});
            skLineSegment(sketch, "E268", {"start": v(-109.42, -109.22) * mm, "end": v(-107.64, -105.79) * mm});
            skArc(sketch, "E269", {"start": v(-103.11, -109.02) * mm, "mid": v(-103.81, -108.68) * mm, "end": v(-104.58, -108.8) * mm});
            skLineSegment(sketch, "E270", {"start": v(-108, -110.63) * mm, "end": v(-104.58, -108.8) * mm});
            skArc(sketch, "E271", {"start": v(-104.44, -113.99) * mm, "mid": v(-103.7, -114.66) * mm, "end": v(-102.96, -115.33) * mm});
            skArc(sketch, "E272", {"start": v(-102.82, -110.48) * mm, "mid": v(-102.73, -109.7) * mm, "end": v(-103.11, -109.02) * mm});
            skLineSegment(sketch, "E273", {"start": v(-104.44, -113.99) * mm, "end": v(-102.82, -110.48) * mm});
            skArc(sketch, "E274", {"start": v(-98.16, -113.5) * mm, "mid": v(-98.87, -113.2) * mm, "end": v(-99.63, -113.36) * mm});
            skLineSegment(sketch, "E275", {"start": v(-102.96, -115.33) * mm, "end": v(-99.63, -113.36) * mm});
            skArc(sketch, "E276", {"start": v(-99.26, -118.53) * mm, "mid": v(-98.5, -119.17) * mm, "end": v(-97.72, -119.8) * mm});
            skArc(sketch, "E277", {"start": v(-97.8, -114.95) * mm, "mid": v(-97.74, -114.17) * mm, "end": v(-98.16, -113.5) * mm});
            skLineSegment(sketch, "E278", {"start": v(-99.26, -118.53) * mm, "end": v(-97.8, -114.95) * mm});
            skArc(sketch, "E279", {"start": v(-93, -117.77) * mm, "mid": v(-93.73, -117.48) * mm, "end": v(-94.48, -117.69) * mm});
            skLineSegment(sketch, "E280", {"start": v(-97.72, -119.8) * mm, "end": v(-94.48, -117.69) * mm});
            skArc(sketch, "E281", {"start": v(-93.88, -122.83) * mm, "mid": v(-93.09, -123.43) * mm, "end": v(-92.29, -124.03) * mm});
            skArc(sketch, "E282", {"start": v(-92.58, -119.19) * mm, "mid": v(-92.56, -118.4) * mm, "end": v(-93, -117.77) * mm});
            skLineSegment(sketch, "E283", {"start": v(-93.88, -122.83) * mm, "end": v(-92.58, -119.19) * mm});
            skArc(sketch, "E284", {"start": v(-87.66, -121.8) * mm, "mid": v(-88.4, -121.54) * mm, "end": v(-89.14, -121.78) * mm});
            skLineSegment(sketch, "E285", {"start": v(-92.29, -124.03) * mm, "end": v(-89.14, -121.78) * mm});
            skArc(sketch, "E286", {"start": v(-88.32, -126.89) * mm, "mid": v(-87.5, -127.46) * mm, "end": v(-86.67, -128.02) * mm});
            skArc(sketch, "E287", {"start": v(-87.18, -123.2) * mm, "mid": v(-87.19, -122.42) * mm, "end": v(-87.66, -121.8) * mm});
            skLineSegment(sketch, "E288", {"start": v(-88.32, -126.89) * mm, "end": v(-87.18, -123.2) * mm});
            skArc(sketch, "E289", {"start": v(-82.15, -125.58) * mm, "mid": v(-82.9, -125.36) * mm, "end": v(-83.63, -125.63) * mm});
            skLineSegment(sketch, "E290", {"start": v(-86.67, -128.02) * mm, "end": v(-83.63, -125.63) * mm});
            skArc(sketch, "E291", {"start": v(-82.58, -130.7) * mm, "mid": v(-81.73, -131.23) * mm, "end": v(-80.88, -131.76) * mm});
            skArc(sketch, "E292", {"start": v(-81.6, -126.96) * mm, "mid": v(-81.65, -126.18) * mm, "end": v(-82.15, -125.58) * mm});
            skLineSegment(sketch, "E293", {"start": v(-82.58, -130.7) * mm, "end": v(-81.6, -126.96) * mm});
            skArc(sketch, "E294", {"start": v(-76.47, -129.11) * mm, "mid": v(-77.23, -128.93) * mm, "end": v(-77.95, -129.23) * mm});
            skLineSegment(sketch, "E295", {"start": v(-80.88, -131.76) * mm, "end": v(-77.95, -129.23) * mm});
            skArc(sketch, "E296", {"start": v(-76.67, -134.25) * mm, "mid": v(-75.8, -134.74) * mm, "end": v(-74.93, -135.23) * mm});
            skArc(sketch, "E297", {"start": v(-75.87, -130.47) * mm, "mid": v(-75.95, -129.69) * mm, "end": v(-76.47, -129.11) * mm});
            skLineSegment(sketch, "E298", {"start": v(-76.67, -134.25) * mm, "end": v(-75.87, -130.47) * mm});
            skArc(sketch, "E299", {"start": v(-70.65, -132.4) * mm, "mid": v(-71.41, -132.24) * mm, "end": v(-72.12, -132.57) * mm});
            skLineSegment(sketch, "E300", {"start": v(-74.93, -135.23) * mm, "end": v(-72.12, -132.57) * mm});
            skArc(sketch, "E301", {"start": v(-70.62, -137.53) * mm, "mid": v(-69.73, -137.98) * mm, "end": v(-68.83, -138.43) * mm});
            skArc(sketch, "E302", {"start": v(-69.98, -133.72) * mm, "mid": v(-70.1, -132.94) * mm, "end": v(-70.65, -132.4) * mm});
            skLineSegment(sketch, "E303", {"start": v(-70.62, -137.53) * mm, "end": v(-69.98, -133.72) * mm});
            skArc(sketch, "E304", {"start": v(-64.68, -135.4) * mm, "mid": v(-65.45, -135.3) * mm, "end": v(-66.14, -135.65) * mm});
            skLineSegment(sketch, "E305", {"start": v(-68.83, -138.43) * mm, "end": v(-66.14, -135.65) * mm});
            skArc(sketch, "E306", {"start": v(-64.42, -140.54) * mm, "mid": v(-63.51, -140.95) * mm, "end": v(-62.6, -141.36) * mm});
            skArc(sketch, "E307", {"start": v(-63.95, -136.7) * mm, "mid": v(-64.1, -135.93) * mm, "end": v(-64.68, -135.4) * mm});
            skLineSegment(sketch, "E308", {"start": v(-64.42, -140.54) * mm, "end": v(-63.95, -136.7) * mm});
            skArc(sketch, "E309", {"start": v(-58.58, -138.16) * mm, "mid": v(-59.36, -138.07) * mm, "end": v(-60.03, -138.47) * mm});
            skLineSegment(sketch, "E310", {"start": v(-62.6, -141.36) * mm, "end": v(-60.03, -138.47) * mm});
            skArc(sketch, "E311", {"start": v(-58.1, -143.27) * mm, "mid": v(-57.17, -143.64) * mm, "end": v(-56.24, -144) * mm});
            skArc(sketch, "E312", {"start": v(-57.8, -139.41) * mm, "mid": v(-57.98, -138.66) * mm, "end": v(-58.58, -138.16) * mm});
            skLineSegment(sketch, "E313", {"start": v(-58.1, -143.27) * mm, "end": v(-57.8, -139.41) * mm});
            skArc(sketch, "E314", {"start": v(-52.37, -140.63) * mm, "mid": v(-53.15, -140.58) * mm, "end": v(-53.8, -141) * mm});
            skLineSegment(sketch, "E315", {"start": v(-56.24, -144) * mm, "end": v(-53.8, -141) * mm});
            skArc(sketch, "E316", {"start": v(-51.66, -145.71) * mm, "mid": v(-50.71, -146.05) * mm, "end": v(-49.77, -146.37) * mm});
            skArc(sketch, "E317", {"start": v(-51.53, -141.85) * mm, "mid": v(-51.75, -141.1) * mm, "end": v(-52.37, -140.63) * mm});
            skLineSegment(sketch, "E318", {"start": v(-51.66, -145.71) * mm, "end": v(-51.53, -141.85) * mm});
            skArc(sketch, "E319", {"start": v(-46.05, -142.82) * mm, "mid": v(-46.83, -142.8) * mm, "end": v(-47.47, -143.26) * mm});
            skLineSegment(sketch, "E320", {"start": v(-49.77, -146.37) * mm, "end": v(-47.47, -143.26) * mm});
            skArc(sketch, "E321", {"start": v(-45.11, -147.87) * mm, "mid": v(-44.16, -148.16) * mm, "end": v(-43.2, -148.44) * mm});
            skArc(sketch, "E322", {"start": v(-45.16, -144) * mm, "mid": v(-45.41, -143.27) * mm, "end": v(-46.05, -142.82) * mm});
            skLineSegment(sketch, "E323", {"start": v(-45.11, -147.87) * mm, "end": v(-45.16, -144) * mm});
            skArc(sketch, "E324", {"start": v(-39.65, -144.73) * mm, "mid": v(-40.43, -144.75) * mm, "end": v(-41.04, -145.23) * mm});
            skLineSegment(sketch, "E325", {"start": v(-43.2, -148.44) * mm, "end": v(-41.04, -145.23) * mm});
            skArc(sketch, "E326", {"start": v(-38.48, -149.73) * mm, "mid": v(-37.51, -149.98) * mm, "end": v(-36.54, -150.22) * mm});
            skArc(sketch, "E327", {"start": v(-38.7, -145.87) * mm, "mid": v(-38.99, -145.15) * mm, "end": v(-39.65, -144.73) * mm});
            skLineSegment(sketch, "E328", {"start": v(-38.48, -149.73) * mm, "end": v(-38.7, -145.87) * mm});
            skArc(sketch, "E329", {"start": v(-33.16, -146.35) * mm, "mid": v(-33.94, -146.4) * mm, "end": v(-34.53, -146.92) * mm});
            skLineSegment(sketch, "E330", {"start": v(-36.54, -150.22) * mm, "end": v(-34.53, -146.92) * mm});
            skArc(sketch, "E331", {"start": v(-31.77, -151.3) * mm, "mid": v(-30.8, -151.5) * mm, "end": v(-29.81, -151.7) * mm});
            skArc(sketch, "E332", {"start": v(-32.16, -147.45) * mm, "mid": v(-32.48, -146.74) * mm, "end": v(-33.16, -146.35) * mm});
            skLineSegment(sketch, "E333", {"start": v(-31.77, -151.3) * mm, "end": v(-32.16, -147.45) * mm});
            skArc(sketch, "E334", {"start": v(-26.6, -147.69) * mm, "mid": v(-27.38, -147.78) * mm, "end": v(-27.95, -148.3) * mm});
            skLineSegment(sketch, "E335", {"start": v(-29.81, -151.7) * mm, "end": v(-27.95, -148.3) * mm});
            skArc(sketch, "E336", {"start": v(-25, -152.56) * mm, "mid": v(-24.01, -152.72) * mm, "end": v(-23.03, -152.88) * mm});
            skArc(sketch, "E337", {"start": v(-25.56, -148.74) * mm, "mid": v(-25.91, -148.04) * mm, "end": v(-26.6, -147.69) * mm});
            skLineSegment(sketch, "E338", {"start": v(-25, -152.56) * mm, "end": v(-25.56, -148.74) * mm});
            skArc(sketch, "E339", {"start": v(-20, -148.72) * mm, "mid": v(-20.77, -148.85) * mm, "end": v(-21.32, -149.4) * mm});
            skLineSegment(sketch, "E340", {"start": v(-23.03, -152.88) * mm, "end": v(-21.32, -149.4) * mm});
            skArc(sketch, "E341", {"start": v(-18.18, -153.53) * mm, "mid": v(-17.19, -153.64) * mm, "end": v(-16.2, -153.75) * mm});
            skArc(sketch, "E342", {"start": v(-18.91, -149.73) * mm, "mid": v(-19.3, -149.05) * mm, "end": v(-20, -148.72) * mm});
            skLineSegment(sketch, "E343", {"start": v(-18.18, -153.53) * mm, "end": v(-18.91, -149.73) * mm});
            skArc(sketch, "E344", {"start": v(-13.36, -149.47) * mm, "mid": v(-14.12, -149.63) * mm, "end": v(-14.64, -150.2) * mm});
            skLineSegment(sketch, "E345", {"start": v(-16.2, -153.75) * mm, "end": v(-14.64, -150.2) * mm});
            skArc(sketch, "E346", {"start": v(-11.32, -154.18) * mm, "mid": v(-10.33, -154.25) * mm, "end": v(-9.33, -154.32) * mm});
            skArc(sketch, "E347", {"start": v(-12.22, -150.42) * mm, "mid": v(-12.63, -149.76) * mm, "end": v(-13.36, -149.47) * mm});
            skLineSegment(sketch, "E348", {"start": v(-11.32, -154.18) * mm, "end": v(-12.22, -150.42) * mm});
            skArc(sketch, "E349", {"start": v(-6.68, -149.91) * mm, "mid": v(-7.44, -150.1) * mm, "end": v(-7.93, -150.71) * mm});
            skLineSegment(sketch, "E350", {"start": v(-9.33, -154.32) * mm, "end": v(-7.93, -150.71) * mm});
            skArc(sketch, "E351", {"start": v(-4.45, -154.54) * mm, "mid": v(-3.44, -154.56) * mm, "end": v(-2.44, -154.58) * mm});
            skArc(sketch, "E352", {"start": v(-5.51, -150.82) * mm, "mid": v(-5.95, -150.17) * mm, "end": v(-6.68, -149.91) * mm});
            skLineSegment(sketch, "E353", {"start": v(-4.45, -154.54) * mm, "end": v(-5.51, -150.82) * mm});
            skArc(sketch, "E354", {"start": v(0, -150.06) * mm, "mid": v(-0.75, -150.29) * mm, "end": v(-1.21, -150.91) * mm});
            skLineSegment(sketch, "E355", {"start": v(-2.44, -154.58) * mm, "end": v(-1.21, -150.91) * mm});
            skArc(sketch, "E356", {"start": v(2.44, -154.58) * mm, "mid": v(3.44, -154.56) * mm, "end": v(4.45, -154.54) * mm});
            skArc(sketch, "E357", {"start": v(1.21, -150.91) * mm, "mid": v(0.75, -150.29) * mm, "end": v(0, -150.06) * mm});
            skLineSegment(sketch, "E358", {"start": v(2.44, -154.58) * mm, "end": v(1.21, -150.91) * mm});
            skArc(sketch, "E359", {"start": v(6.68, -149.91) * mm, "mid": v(5.95, -150.17) * mm, "end": v(5.51, -150.82) * mm});
            skLineSegment(sketch, "E360", {"start": v(4.45, -154.54) * mm, "end": v(5.51, -150.82) * mm});
            skArc(sketch, "E361", {"start": v(9.33, -154.32) * mm, "mid": v(10.33, -154.25) * mm, "end": v(11.32, -154.18) * mm});
            skArc(sketch, "E362", {"start": v(7.93, -150.71) * mm, "mid": v(7.44, -150.1) * mm, "end": v(6.68, -149.91) * mm});
            skLineSegment(sketch, "E363", {"start": v(9.33, -154.32) * mm, "end": v(7.93, -150.71) * mm});
            skArc(sketch, "E364", {"start": v(13.36, -149.47) * mm, "mid": v(12.63, -149.76) * mm, "end": v(12.22, -150.42) * mm});
            skLineSegment(sketch, "E365", {"start": v(11.32, -154.18) * mm, "end": v(12.22, -150.42) * mm});
            skArc(sketch, "E366", {"start": v(16.2, -153.75) * mm, "mid": v(17.19, -153.64) * mm, "end": v(18.18, -153.53) * mm});
            skArc(sketch, "E367", {"start": v(14.64, -150.2) * mm, "mid": v(14.12, -149.63) * mm, "end": v(13.36, -149.47) * mm});
            skLineSegment(sketch, "E368", {"start": v(16.2, -153.75) * mm, "end": v(14.64, -150.2) * mm});
            skArc(sketch, "E369", {"start": v(20, -148.72) * mm, "mid": v(19.3, -149.05) * mm, "end": v(18.91, -149.73) * mm});
            skLineSegment(sketch, "E370", {"start": v(18.18, -153.53) * mm, "end": v(18.91, -149.73) * mm});
            skArc(sketch, "E371", {"start": v(23.03, -152.88) * mm, "mid": v(24.01, -152.72) * mm, "end": v(25, -152.56) * mm});
            skArc(sketch, "E372", {"start": v(21.32, -149.4) * mm, "mid": v(20.77, -148.85) * mm, "end": v(20, -148.72) * mm});
            skLineSegment(sketch, "E373", {"start": v(23.03, -152.88) * mm, "end": v(21.32, -149.4) * mm});
            skArc(sketch, "E374", {"start": v(26.6, -147.69) * mm, "mid": v(25.91, -148.04) * mm, "end": v(25.56, -148.74) * mm});
            skLineSegment(sketch, "E375", {"start": v(25, -152.56) * mm, "end": v(25.56, -148.74) * mm});
            skArc(sketch, "E376", {"start": v(29.81, -151.7) * mm, "mid": v(30.8, -151.5) * mm, "end": v(31.77, -151.3) * mm});
            skArc(sketch, "E377", {"start": v(27.95, -148.3) * mm, "mid": v(27.38, -147.78) * mm, "end": v(26.6, -147.69) * mm});
            skLineSegment(sketch, "E378", {"start": v(29.81, -151.7) * mm, "end": v(27.95, -148.3) * mm});
            skArc(sketch, "E379", {"start": v(33.16, -146.35) * mm, "mid": v(32.48, -146.74) * mm, "end": v(32.16, -147.45) * mm});
            skLineSegment(sketch, "E380", {"start": v(31.77, -151.3) * mm, "end": v(32.16, -147.45) * mm});
            skArc(sketch, "E381", {"start": v(36.54, -150.22) * mm, "mid": v(37.51, -149.98) * mm, "end": v(38.48, -149.73) * mm});
            skArc(sketch, "E382", {"start": v(34.53, -146.92) * mm, "mid": v(33.94, -146.4) * mm, "end": v(33.16, -146.35) * mm});
            skLineSegment(sketch, "E383", {"start": v(36.54, -150.22) * mm, "end": v(34.53, -146.92) * mm});
            skArc(sketch, "E384", {"start": v(39.65, -144.73) * mm, "mid": v(38.99, -145.15) * mm, "end": v(38.7, -145.87) * mm});
            skLineSegment(sketch, "E385", {"start": v(38.48, -149.73) * mm, "end": v(38.7, -145.87) * mm});
            skArc(sketch, "E386", {"start": v(43.2, -148.44) * mm, "mid": v(44.16, -148.16) * mm, "end": v(45.11, -147.87) * mm});
            skArc(sketch, "E387", {"start": v(41.04, -145.23) * mm, "mid": v(40.43, -144.75) * mm, "end": v(39.65, -144.73) * mm});
            skLineSegment(sketch, "E388", {"start": v(43.2, -148.44) * mm, "end": v(41.04, -145.23) * mm});
            skArc(sketch, "E389", {"start": v(46.05, -142.82) * mm, "mid": v(45.41, -143.27) * mm, "end": v(45.16, -144) * mm});
            skLineSegment(sketch, "E390", {"start": v(45.11, -147.87) * mm, "end": v(45.16, -144) * mm});
            skArc(sketch, "E391", {"start": v(49.77, -146.37) * mm, "mid": v(50.71, -146.05) * mm, "end": v(51.66, -145.71) * mm});
            skArc(sketch, "E392", {"start": v(47.47, -143.26) * mm, "mid": v(46.83, -142.8) * mm, "end": v(46.05, -142.82) * mm});
            skLineSegment(sketch, "E393", {"start": v(49.77, -146.37) * mm, "end": v(47.47, -143.26) * mm});
            skArc(sketch, "E394", {"start": v(52.37, -140.63) * mm, "mid": v(51.75, -141.1) * mm, "end": v(51.53, -141.85) * mm});
            skLineSegment(sketch, "E395", {"start": v(51.66, -145.71) * mm, "end": v(51.53, -141.85) * mm});
            skArc(sketch, "E396", {"start": v(56.24, -144) * mm, "mid": v(57.17, -143.64) * mm, "end": v(58.1, -143.27) * mm});
            skArc(sketch, "E397", {"start": v(53.8, -141) * mm, "mid": v(53.15, -140.58) * mm, "end": v(52.37, -140.63) * mm});
            skLineSegment(sketch, "E398", {"start": v(56.24, -144) * mm, "end": v(53.8, -141) * mm});
            skArc(sketch, "E399", {"start": v(58.58, -138.16) * mm, "mid": v(57.98, -138.66) * mm, "end": v(57.8, -139.41) * mm});
            skLineSegment(sketch, "E400", {"start": v(58.1, -143.27) * mm, "end": v(57.8, -139.41) * mm});
            skArc(sketch, "E401", {"start": v(62.6, -141.36) * mm, "mid": v(63.51, -140.95) * mm, "end": v(64.42, -140.54) * mm});
            skArc(sketch, "E402", {"start": v(60.03, -138.47) * mm, "mid": v(59.36, -138.07) * mm, "end": v(58.58, -138.16) * mm});
            skLineSegment(sketch, "E403", {"start": v(62.6, -141.36) * mm, "end": v(60.03, -138.47) * mm});
            skArc(sketch, "E404", {"start": v(64.68, -135.4) * mm, "mid": v(64.1, -135.93) * mm, "end": v(63.95, -136.7) * mm});
            skLineSegment(sketch, "E405", {"start": v(64.42, -140.54) * mm, "end": v(63.95, -136.7) * mm});
            skArc(sketch, "E406", {"start": v(68.83, -138.43) * mm, "mid": v(69.73, -137.98) * mm, "end": v(70.62, -137.53) * mm});
            skArc(sketch, "E407", {"start": v(66.14, -135.65) * mm, "mid": v(65.45, -135.3) * mm, "end": v(64.68, -135.4) * mm});
            skLineSegment(sketch, "E408", {"start": v(68.83, -138.43) * mm, "end": v(66.14, -135.65) * mm});
            skArc(sketch, "E409", {"start": v(70.65, -132.4) * mm, "mid": v(70.1, -132.94) * mm, "end": v(69.98, -133.72) * mm});
            skLineSegment(sketch, "E410", {"start": v(70.62, -137.53) * mm, "end": v(69.98, -133.72) * mm});
            skArc(sketch, "E411", {"start": v(74.93, -135.23) * mm, "mid": v(75.8, -134.74) * mm, "end": v(76.67, -134.25) * mm});
            skArc(sketch, "E412", {"start": v(72.12, -132.57) * mm, "mid": v(71.41, -132.24) * mm, "end": v(70.65, -132.4) * mm});
            skLineSegment(sketch, "E413", {"start": v(74.93, -135.23) * mm, "end": v(72.12, -132.57) * mm});
            skArc(sketch, "E414", {"start": v(76.47, -129.11) * mm, "mid": v(75.95, -129.69) * mm, "end": v(75.87, -130.47) * mm});
            skLineSegment(sketch, "E415", {"start": v(76.67, -134.25) * mm, "end": v(75.87, -130.47) * mm});
            skArc(sketch, "E416", {"start": v(80.88, -131.76) * mm, "mid": v(81.73, -131.23) * mm, "end": v(82.58, -130.7) * mm});
            skArc(sketch, "E417", {"start": v(77.95, -129.23) * mm, "mid": v(77.23, -128.93) * mm, "end": v(76.47, -129.11) * mm});
            skLineSegment(sketch, "E418", {"start": v(80.88, -131.76) * mm, "end": v(77.95, -129.23) * mm});
            skArc(sketch, "E419", {"start": v(82.15, -125.58) * mm, "mid": v(81.65, -126.18) * mm, "end": v(81.6, -126.96) * mm});
            skLineSegment(sketch, "E420", {"start": v(82.58, -130.7) * mm, "end": v(81.6, -126.96) * mm});
            skArc(sketch, "E421", {"start": v(86.67, -128.02) * mm, "mid": v(87.5, -127.46) * mm, "end": v(88.32, -126.89) * mm});
            skArc(sketch, "E422", {"start": v(83.63, -125.63) * mm, "mid": v(82.9, -125.36) * mm, "end": v(82.15, -125.58) * mm});
            skLineSegment(sketch, "E423", {"start": v(86.67, -128.02) * mm, "end": v(83.63, -125.63) * mm});
            skArc(sketch, "E424", {"start": v(87.66, -121.8) * mm, "mid": v(87.19, -122.42) * mm, "end": v(87.18, -123.2) * mm});
            skLineSegment(sketch, "E425", {"start": v(88.32, -126.89) * mm, "end": v(87.18, -123.2) * mm});
            skArc(sketch, "E426", {"start": v(92.29, -124.03) * mm, "mid": v(93.09, -123.43) * mm, "end": v(93.88, -122.83) * mm});
            skArc(sketch, "E427", {"start": v(89.14, -121.78) * mm, "mid": v(88.4, -121.54) * mm, "end": v(87.66, -121.8) * mm});
            skLineSegment(sketch, "E428", {"start": v(92.29, -124.03) * mm, "end": v(89.14, -121.78) * mm});
            skArc(sketch, "E429", {"start": v(93, -117.77) * mm, "mid": v(92.56, -118.4) * mm, "end": v(92.58, -119.19) * mm});
            skLineSegment(sketch, "E430", {"start": v(93.88, -122.83) * mm, "end": v(92.58, -119.19) * mm});
            skArc(sketch, "E431", {"start": v(97.72, -119.8) * mm, "mid": v(98.5, -119.17) * mm, "end": v(99.26, -118.53) * mm});
            skArc(sketch, "E432", {"start": v(94.48, -117.69) * mm, "mid": v(93.73, -117.48) * mm, "end": v(93, -117.77) * mm});
            skLineSegment(sketch, "E433", {"start": v(97.72, -119.8) * mm, "end": v(94.48, -117.69) * mm});
            skArc(sketch, "E434", {"start": v(98.16, -113.5) * mm, "mid": v(97.74, -114.17) * mm, "end": v(97.8, -114.95) * mm});
            skLineSegment(sketch, "E435", {"start": v(99.26, -118.53) * mm, "end": v(97.8, -114.95) * mm});
            skArc(sketch, "E436", {"start": v(102.96, -115.33) * mm, "mid": v(103.7, -114.66) * mm, "end": v(104.44, -113.99) * mm});
            skArc(sketch, "E437", {"start": v(99.63, -113.36) * mm, "mid": v(98.87, -113.2) * mm, "end": v(98.16, -113.5) * mm});
            skLineSegment(sketch, "E438", {"start": v(102.96, -115.33) * mm, "end": v(99.63, -113.36) * mm});
            skArc(sketch, "E439", {"start": v(103.11, -109.02) * mm, "mid": v(102.73, -109.7) * mm, "end": v(102.82, -110.48) * mm});
            skLineSegment(sketch, "E440", {"start": v(104.44, -113.99) * mm, "end": v(102.82, -110.48) * mm});
            skArc(sketch, "E441", {"start": v(108, -110.63) * mm, "mid": v(108.7, -109.93) * mm, "end": v(109.42, -109.22) * mm});
            skArc(sketch, "E442", {"start": v(104.58, -108.8) * mm, "mid": v(103.81, -108.68) * mm, "end": v(103.11, -109.02) * mm});
            skLineSegment(sketch, "E443", {"start": v(108, -110.63) * mm, "end": v(104.58, -108.8) * mm});
            skArc(sketch, "E444", {"start": v(107.87, -104.32) * mm, "mid": v(107.51, -105.02) * mm, "end": v(107.64, -105.79) * mm});
            skLineSegment(sketch, "E445", {"start": v(109.42, -109.22) * mm, "end": v(107.64, -105.79) * mm});
            skArc(sketch, "E446", {"start": v(112.81, -105.7) * mm, "mid": v(113.5, -104.97) * mm, "end": v(114.17, -104.24) * mm});
            skArc(sketch, "E447", {"start": v(109.32, -104.04) * mm, "mid": v(108.55, -103.94) * mm, "end": v(107.87, -104.32) * mm});
            skLineSegment(sketch, "E448", {"start": v(112.81, -105.7) * mm, "end": v(109.32, -104.04) * mm});
            skArc(sketch, "E449", {"start": v(112.4, -99.41) * mm, "mid": v(112.08, -100.12) * mm, "end": v(112.24, -100.89) * mm});
            skLineSegment(sketch, "E450", {"start": v(114.17, -104.24) * mm, "end": v(112.24, -100.89) * mm});
            skArc(sketch, "E451", {"start": v(117.41, -100.58) * mm, "mid": v(118.06, -99.81) * mm, "end": v(118.7, -99.05) * mm});
            skArc(sketch, "E452", {"start": v(113.85, -99.07) * mm, "mid": v(113.07, -99) * mm, "end": v(112.4, -99.41) * mm});
            skLineSegment(sketch, "E453", {"start": v(117.41, -100.58) * mm, "end": v(113.85, -99.07) * mm});
            skArc(sketch, "E454", {"start": v(116.73, -94.3) * mm, "mid": v(116.43, -95.03) * mm, "end": v(116.63, -95.79) * mm});
            skLineSegment(sketch, "E455", {"start": v(118.7, -99.05) * mm, "end": v(116.63, -95.79) * mm});
            skArc(sketch, "E456", {"start": v(121.78, -95.25) * mm, "mid": v(122.39, -94.46) * mm, "end": v(123, -93.66) * mm});
            skArc(sketch, "E457", {"start": v(118.15, -93.9) * mm, "mid": v(117.37, -93.87) * mm, "end": v(116.73, -94.3) * mm});
            skLineSegment(sketch, "E458", {"start": v(121.78, -95.25) * mm, "end": v(118.15, -93.9) * mm});
            skArc(sketch, "E459", {"start": v(120.81, -89.01) * mm, "mid": v(120.55, -89.75) * mm, "end": v(120.78, -90.5) * mm});
            skLineSegment(sketch, "E460", {"start": v(123, -93.66) * mm, "end": v(120.78, -90.5) * mm});
            skArc(sketch, "E461", {"start": v(125.9, -89.73) * mm, "mid": v(126.48, -88.9) * mm, "end": v(127.05, -88.09) * mm});
            skArc(sketch, "E462", {"start": v(122.22, -88.54) * mm, "mid": v(121.44, -88.55) * mm, "end": v(120.81, -89.01) * mm});
            skLineSegment(sketch, "E463", {"start": v(125.9, -89.73) * mm, "end": v(122.22, -88.54) * mm});
            skArc(sketch, "E464", {"start": v(124.66, -83.54) * mm, "mid": v(124.43, -84.3) * mm, "end": v(124.69, -85.03) * mm});
            skLineSegment(sketch, "E465", {"start": v(127.05, -88.09) * mm, "end": v(124.69, -85.03) * mm});
            skArc(sketch, "E466", {"start": v(129.77, -84.03) * mm, "mid": v(130.31, -83.19) * mm, "end": v(130.85, -82.34) * mm});
            skArc(sketch, "E467", {"start": v(126.04, -83.01) * mm, "mid": v(125.26, -83.05) * mm, "end": v(124.66, -83.54) * mm});
            skLineSegment(sketch, "E468", {"start": v(129.77, -84.03) * mm, "end": v(126.04, -83.01) * mm});
            skArc(sketch, "E469", {"start": v(128.25, -77.9) * mm, "mid": v(128.06, -78.66) * mm, "end": v(128.35, -79.39) * mm});
            skLineSegment(sketch, "E470", {"start": v(130.85, -82.34) * mm, "end": v(128.35, -79.39) * mm});
            skArc(sketch, "E471", {"start": v(133.38, -78.17) * mm, "mid": v(133.89, -77.3) * mm, "end": v(134.39, -76.43) * mm});
            skArc(sketch, "E472", {"start": v(129.61, -77.31) * mm, "mid": v(128.84, -77.39) * mm, "end": v(128.25, -77.9) * mm});
            skLineSegment(sketch, "E473", {"start": v(133.38, -78.17) * mm, "end": v(129.61, -77.31) * mm});
            skArc(sketch, "E474", {"start": v(131.6, -72.12) * mm, "mid": v(131.44, -72.88) * mm, "end": v(131.76, -73.6) * mm});
            skLineSegment(sketch, "E475", {"start": v(134.39, -76.43) * mm, "end": v(131.76, -73.6) * mm});
            skArc(sketch, "E476", {"start": v(136.73, -72.15) * mm, "mid": v(137.2, -71.26) * mm, "end": v(137.66, -70.37) * mm});
            skArc(sketch, "E477", {"start": v(132.93, -71.46) * mm, "mid": v(132.16, -71.57) * mm, "end": v(131.6, -72.12) * mm});
            skLineSegment(sketch, "E478", {"start": v(136.73, -72.15) * mm, "end": v(132.93, -71.46) * mm});
            skArc(sketch, "E479", {"start": v(134.68, -66.18) * mm, "mid": v(134.55, -66.95) * mm, "end": v(134.9, -67.65) * mm});
            skLineSegment(sketch, "E480", {"start": v(137.66, -70.37) * mm, "end": v(134.9, -67.65) * mm});
            skArc(sketch, "E481", {"start": v(139.81, -65.98) * mm, "mid": v(140.24, -65.08) * mm, "end": v(140.65, -64.17) * mm});
            skArc(sketch, "E482", {"start": v(135.98, -65.47) * mm, "mid": v(135.21, -65.61) * mm, "end": v(134.68, -66.18) * mm});
            skLineSegment(sketch, "E483", {"start": v(139.81, -65.98) * mm, "end": v(135.98, -65.47) * mm});
            skArc(sketch, "E484", {"start": v(137.5, -60.12) * mm, "mid": v(137.4, -60.9) * mm, "end": v(137.79, -61.57) * mm});
            skLineSegment(sketch, "E485", {"start": v(140.65, -64.17) * mm, "end": v(137.79, -61.57) * mm});
            skArc(sketch, "E486", {"start": v(142.61, -59.69) * mm, "mid": v(143, -58.76) * mm, "end": v(143.37, -57.84) * mm});
            skArc(sketch, "E487", {"start": v(138.76, -59.35) * mm, "mid": v(138, -59.53) * mm, "end": v(137.5, -60.12) * mm});
            skLineSegment(sketch, "E488", {"start": v(142.61, -59.69) * mm, "end": v(138.76, -59.35) * mm});
            skArc(sketch, "E489", {"start": v(140.04, -53.93) * mm, "mid": v(139.98, -54.71) * mm, "end": v(140.4, -55.37) * mm});
            skLineSegment(sketch, "E490", {"start": v(143.37, -57.84) * mm, "end": v(140.4, -55.37) * mm});
            skArc(sketch, "E491", {"start": v(145.13, -53.28) * mm, "mid": v(145.47, -52.34) * mm, "end": v(145.8, -51.4) * mm});
            skArc(sketch, "E492", {"start": v(141.27, -53.1) * mm, "mid": v(140.52, -53.32) * mm, "end": v(140.04, -53.93) * mm});
            skLineSegment(sketch, "E493", {"start": v(145.13, -53.28) * mm, "end": v(141.27, -53.1) * mm});
            skArc(sketch, "E494", {"start": v(142.3, -47.64) * mm, "mid": v(142.28, -48.42) * mm, "end": v(142.72, -49.06) * mm});
            skLineSegment(sketch, "E495", {"start": v(145.8, -51.4) * mm, "end": v(142.72, -49.06) * mm});
            skArc(sketch, "E496", {"start": v(147.36, -46.76) * mm, "mid": v(147.66, -45.8) * mm, "end": v(147.95, -44.85) * mm});
            skArc(sketch, "E497", {"start": v(143.5, -46.76) * mm, "mid": v(142.75, -47) * mm, "end": v(142.3, -47.64) * mm});
            skLineSegment(sketch, "E498", {"start": v(147.36, -46.76) * mm, "end": v(143.5, -46.76) * mm});
            skArc(sketch, "E499", {"start": v(144.28, -41.26) * mm, "mid": v(144.3, -42.04) * mm, "end": v(144.77, -42.66) * mm});
            skLineSegment(sketch, "E500", {"start": v(147.95, -44.85) * mm, "end": v(144.77, -42.66) * mm});
            skArc(sketch, "E501", {"start": v(149.3, -40.15) * mm, "mid": v(149.55, -39.18) * mm, "end": v(149.8, -38.21) * mm});
            skArc(sketch, "E502", {"start": v(145.43, -40.32) * mm, "mid": v(144.7, -40.6) * mm, "end": v(144.28, -41.26) * mm});
            skLineSegment(sketch, "E503", {"start": v(149.3, -40.15) * mm, "end": v(145.43, -40.32) * mm});
            skArc(sketch, "E504", {"start": v(145.97, -34.79) * mm, "mid": v(146.02, -35.57) * mm, "end": v(146.52, -36.16) * mm});
            skLineSegment(sketch, "E505", {"start": v(149.8, -38.21) * mm, "end": v(146.52, -36.16) * mm});
            skArc(sketch, "E506", {"start": v(150.94, -33.46) * mm, "mid": v(151.15, -32.48) * mm, "end": v(151.36, -31.5) * mm});
            skArc(sketch, "E507", {"start": v(147.08, -33.8) * mm, "mid": v(146.37, -34.11) * mm, "end": v(145.97, -34.79) * mm});
            skLineSegment(sketch, "E508", {"start": v(150.94, -33.46) * mm, "end": v(147.08, -33.8) * mm});
            skArc(sketch, "E509", {"start": v(147.38, -28.25) * mm, "mid": v(147.46, -29.03) * mm, "end": v(147.99, -29.6) * mm});
            skLineSegment(sketch, "E510", {"start": v(151.36, -31.5) * mm, "end": v(147.99, -29.6) * mm});
            skArc(sketch, "E511", {"start": v(152.28, -26.7) * mm, "mid": v(152.45, -25.71) * mm, "end": v(152.6, -24.73) * mm});
            skArc(sketch, "E512", {"start": v(148.44, -27.22) * mm, "mid": v(147.74, -27.56) * mm, "end": v(147.38, -28.25) * mm});
            skLineSegment(sketch, "E513", {"start": v(152.28, -26.7) * mm, "end": v(148.44, -27.22) * mm});
            skArc(sketch, "E514", {"start": v(148.5, -21.66) * mm, "mid": v(148.6, -22.43) * mm, "end": v(149.16, -22.98) * mm});
            skLineSegment(sketch, "E515", {"start": v(152.6, -24.73) * mm, "end": v(149.16, -22.98) * mm});
            skArc(sketch, "E516", {"start": v(153.32, -19.9) * mm, "mid": v(153.44, -18.9) * mm, "end": v(153.56, -17.9) * mm});
            skArc(sketch, "E517", {"start": v(149.5, -20.58) * mm, "mid": v(148.82, -20.95) * mm, "end": v(148.5, -21.66) * mm});
            skLineSegment(sketch, "E518", {"start": v(153.32, -19.9) * mm, "end": v(149.5, -20.58) * mm});
            skArc(sketch, "E519", {"start": v(149.3, -15.02) * mm, "mid": v(149.46, -15.79) * mm, "end": v(150.04, -16.31) * mm});
            skLineSegment(sketch, "E520", {"start": v(153.56, -17.9) * mm, "end": v(150.04, -16.31) * mm});
            skArc(sketch, "E521", {"start": v(154.05, -13.04) * mm, "mid": v(154.13, -12.04) * mm, "end": v(154.2, -11.05) * mm});
            skArc(sketch, "E522", {"start": v(150.28, -13.9) * mm, "mid": v(149.6, -14.3) * mm, "end": v(149.3, -15.02) * mm});
            skLineSegment(sketch, "E523", {"start": v(154.05, -13.04) * mm, "end": v(150.28, -13.9) * mm});
            skArc(sketch, "E524", {"start": v(149.83, -8.35) * mm, "mid": v(150.01, -9.11) * mm, "end": v(150.61, -9.61) * mm});
            skLineSegment(sketch, "E525", {"start": v(154.2, -11.05) * mm, "end": v(150.61, -9.61) * mm});
            skArc(sketch, "E526", {"start": v(154.48, -6.17) * mm, "mid": v(154.51, -5.17) * mm, "end": v(154.54, -4.17) * mm});
            skArc(sketch, "E527", {"start": v(150.75, -7.2) * mm, "mid": v(150.1, -7.62) * mm, "end": v(149.83, -8.35) * mm});
            skLineSegment(sketch, "E528", {"start": v(154.48, -6.17) * mm, "end": v(150.75, -7.2) * mm});
            skArc(sketch, "E529", {"start": v(150.05, -1.67) * mm, "mid": v(150.27, -2.42) * mm, "end": v(150.9, -2.9) * mm});
            skLineSegment(sketch, "E530", {"start": v(154.54, -4.17) * mm, "end": v(150.9, -2.9) * mm});
            skArc(sketch, "E531", {"start": v(154.6, 0.72) * mm, "mid": v(154.6, 1.72) * mm, "end": v(154.58, 2.72) * mm});
            skArc(sketch, "E532", {"start": v(150.92, -0.47) * mm, "mid": v(150.29, -0.93) * mm, "end": v(150.05, -1.67) * mm});
            skLineSegment(sketch, "E533", {"start": v(154.6, 0.72) * mm, "end": v(150.92, -0.47) * mm});
            skArc(sketch, "E534", {"start": v(149.98, 5.01) * mm, "mid": v(150.23, 4.28) * mm, "end": v(150.87, 3.83) * mm});
            skLineSegment(sketch, "E535", {"start": v(154.58, 2.72) * mm, "end": v(150.87, 3.83) * mm});
            skArc(sketch, "E536", {"start": v(154.41, 7.6) * mm, "mid": v(154.36, 8.6) * mm, "end": v(154.3, 9.6) * mm});
            skArc(sketch, "E537", {"start": v(150.79, 6.25) * mm, "mid": v(150.18, 5.77) * mm, "end": v(149.98, 5.01) * mm});
            skLineSegment(sketch, "E538", {"start": v(154.41, 7.6) * mm, "end": v(150.79, 6.25) * mm});
            skArc(sketch, "E539", {"start": v(149.6, 11.7) * mm, "mid": v(149.9, 10.96) * mm, "end": v(150.55, 10.55) * mm});
            skLineSegment(sketch, "E540", {"start": v(154.3, 9.6) * mm, "end": v(150.55, 10.55) * mm});
            skArc(sketch, "E541", {"start": v(153.92, 14.48) * mm, "mid": v(153.82, 15.47) * mm, "end": v(153.72, 16.47) * mm});
            skArc(sketch, "E542", {"start": v(150.36, 12.97) * mm, "mid": v(149.77, 12.45) * mm, "end": v(149.6, 11.7) * mm});
            skLineSegment(sketch, "E543", {"start": v(153.92, 14.48) * mm, "end": v(150.36, 12.97) * mm});
            skArc(sketch, "E544", {"start": v(148.94, 18.34) * mm, "mid": v(149.25, 17.63) * mm, "end": v(149.93, 17.24) * mm});
            skLineSegment(sketch, "E545", {"start": v(153.72, 16.47) * mm, "end": v(149.93, 17.24) * mm});
            skArc(sketch, "E546", {"start": v(153.12, 21.32) * mm, "mid": v(152.98, 22.31) * mm, "end": v(152.83, 23.3) * mm});
            skArc(sketch, "E547", {"start": v(149.63, 19.65) * mm, "mid": v(149.07, 19.11) * mm, "end": v(148.94, 18.34) * mm});
            skLineSegment(sketch, "E548", {"start": v(153.12, 21.32) * mm, "end": v(149.63, 19.65) * mm});
            skArc(sketch, "E549", {"start": v(147.97, 24.96) * mm, "mid": v(148.32, 24.26) * mm, "end": v(149.01, 23.9) * mm});
            skLineSegment(sketch, "E550", {"start": v(152.83, 23.3) * mm, "end": v(149.01, 23.9) * mm});
            skArc(sketch, "E551", {"start": v(152.02, 28.12) * mm, "mid": v(151.84, 29.1) * mm, "end": v(151.64, 30.09) * mm});
            skArc(sketch, "E552", {"start": v(148.61, 26.3) * mm, "mid": v(148.07, 25.73) * mm, "end": v(147.97, 24.96) * mm});
            skLineSegment(sketch, "E553", {"start": v(152.02, 28.12) * mm, "end": v(148.61, 26.3) * mm});
            skArc(sketch, "E554", {"start": v(146.71, 31.53) * mm, "mid": v(147.1, 30.84) * mm, "end": v(147.8, 30.52) * mm});
            skLineSegment(sketch, "E555", {"start": v(151.64, 30.09) * mm, "end": v(147.8, 30.52) * mm});
            skArc(sketch, "E556", {"start": v(150.62, 34.86) * mm, "mid": v(150.39, 35.84) * mm, "end": v(150.15, 36.81) * mm});
            skArc(sketch, "E557", {"start": v(147.3, 32.9) * mm, "mid": v(146.78, 32.3) * mm, "end": v(146.71, 31.53) * mm});
            skLineSegment(sketch, "E558", {"start": v(150.62, 34.86) * mm, "end": v(147.3, 32.9) * mm});
            skArc(sketch, "E559", {"start": v(145.16, 38.03) * mm, "mid": v(145.57, 37.37) * mm, "end": v(146.3, 37.07) * mm});
            skLineSegment(sketch, "E560", {"start": v(150.15, 36.81) * mm, "end": v(146.3, 37.07) * mm});
            skArc(sketch, "E561", {"start": v(148.91, 41.54) * mm, "mid": v(148.64, 42.5) * mm, "end": v(148.36, 43.46) * mm});
            skArc(sketch, "E562", {"start": v(145.68, 39.42) * mm, "mid": v(145.2, 38.81) * mm, "end": v(145.16, 38.03) * mm});
            skLineSegment(sketch, "E563", {"start": v(148.91, 41.54) * mm, "end": v(145.68, 39.42) * mm});
            skArc(sketch, "E564", {"start": v(143.33, 44.46) * mm, "mid": v(143.76, 43.81) * mm, "end": v(144.5, 43.55) * mm});
            skLineSegment(sketch, "E565", {"start": v(148.36, 43.46) * mm, "end": v(144.5, 43.55) * mm});
            skArc(sketch, "E566", {"start": v(146.92, 48.13) * mm, "mid": v(146.6, 49.08) * mm, "end": v(146.28, 50.03) * mm});
            skArc(sketch, "E567", {"start": v(143.78, 45.87) * mm, "mid": v(143.32, 45.24) * mm, "end": v(143.33, 44.46) * mm});
            skLineSegment(sketch, "E568", {"start": v(146.92, 48.13) * mm, "end": v(143.78, 45.87) * mm});
            skArc(sketch, "E569", {"start": v(141.2, 50.8) * mm, "mid": v(141.67, 50.18) * mm, "end": v(142.41, 49.95) * mm});
            skLineSegment(sketch, "E570", {"start": v(146.28, 50.03) * mm, "end": v(142.41, 49.95) * mm});
            skArc(sketch, "E571", {"start": v(144.63, 54.63) * mm, "mid": v(144.27, 55.56) * mm, "end": v(143.9, 56.5) * mm});
            skArc(sketch, "E572", {"start": v(141.6, 52.23) * mm, "mid": v(141.16, 51.58) * mm, "end": v(141.2, 50.8) * mm});
            skLineSegment(sketch, "E573", {"start": v(144.63, 54.63) * mm, "end": v(141.6, 52.23) * mm});
            skArc(sketch, "E574", {"start": v(138.8, 57.04) * mm, "mid": v(139.3, 56.44) * mm, "end": v(140.05, 56.24) * mm});
            skLineSegment(sketch, "E575", {"start": v(143.9, 56.5) * mm, "end": v(140.05, 56.24) * mm});
            skArc(sketch, "E576", {"start": v(142.05, 61.02) * mm, "mid": v(141.65, 61.94) * mm, "end": v(141.25, 62.85) * mm});
            skArc(sketch, "E577", {"start": v(139.13, 58.49) * mm, "mid": v(138.73, 57.82) * mm, "end": v(138.8, 57.04) * mm});
            skLineSegment(sketch, "E578", {"start": v(142.05, 61.02) * mm, "end": v(139.13, 58.49) * mm});
            skArc(sketch, "E579", {"start": v(136.12, 63.17) * mm, "mid": v(136.64, 62.59) * mm, "end": v(137.4, 62.43) * mm});
            skLineSegment(sketch, "E580", {"start": v(141.25, 62.85) * mm, "end": v(137.4, 62.43) * mm});
            skArc(sketch, "E581", {"start": v(139.2, 67.28) * mm, "mid": v(138.75, 68.18) * mm, "end": v(138.3, 69.08) * mm});
            skArc(sketch, "E582", {"start": v(136.38, 64.63) * mm, "mid": v(136.01, 63.94) * mm, "end": v(136.12, 63.17) * mm});
            skLineSegment(sketch, "E583", {"start": v(139.2, 67.28) * mm, "end": v(136.38, 64.63) * mm});
            skArc(sketch, "E584", {"start": v(133.17, 69.17) * mm, "mid": v(133.72, 68.6) * mm, "end": v(134.49, 68.48) * mm});
            skLineSegment(sketch, "E585", {"start": v(138.3, 69.08) * mm, "end": v(134.49, 68.48) * mm});
            skArc(sketch, "E586", {"start": v(136.05, 73.42) * mm, "mid": v(135.58, 74.3) * mm, "end": v(135.1, 75.17) * mm});
            skArc(sketch, "E587", {"start": v(133.37, 70.64) * mm, "mid": v(133.03, 69.93) * mm, "end": v(133.17, 69.17) * mm});
            skLineSegment(sketch, "E588", {"start": v(136.05, 73.42) * mm, "end": v(133.37, 70.64) * mm});
            skArc(sketch, "E589", {"start": v(129.96, 75.03) * mm, "mid": v(130.53, 74.5) * mm, "end": v(131.3, 74.4) * mm});
            skLineSegment(sketch, "E590", {"start": v(135.1, 75.17) * mm, "end": v(131.3, 74.4) * mm});
            skArc(sketch, "E591", {"start": v(132.65, 79.4) * mm, "mid": v(132.13, 80.26) * mm, "end": v(131.6, 81.12) * mm});
            skArc(sketch, "E592", {"start": v(130.09, 76.5) * mm, "mid": v(129.78, 75.8) * mm, "end": v(129.96, 75.03) * mm});
            skLineSegment(sketch, "E593", {"start": v(132.65, 79.4) * mm, "end": v(130.09, 76.5) * mm});
            skArc(sketch, "E594", {"start": v(126.49, 80.75) * mm, "mid": v(127.08, 80.24) * mm, "end": v(127.86, 80.18) * mm});
            skLineSegment(sketch, "E595", {"start": v(131.6, 81.12) * mm, "end": v(127.86, 80.18) * mm});
            skArc(sketch, "E596", {"start": v(128.98, 85.24) * mm, "mid": v(128.43, 86.07) * mm, "end": v(127.87, 86.9) * mm});
            skArc(sketch, "E597", {"start": v(126.55, 82.23) * mm, "mid": v(126.28, 81.5) * mm, "end": v(126.49, 80.75) * mm});
            skLineSegment(sketch, "E598", {"start": v(128.98, 85.24) * mm, "end": v(126.55, 82.23) * mm});
            skArc(sketch, "E599", {"start": v(122.76, 86.3) * mm, "mid": v(123.38, 85.82) * mm, "end": v(124.16, 85.8) * mm});
            skLineSegment(sketch, "E600", {"start": v(127.87, 86.9) * mm, "end": v(124.16, 85.8) * mm});
            skArc(sketch, "E601", {"start": v(125.05, 90.9) * mm, "mid": v(124.46, 91.7) * mm, "end": v(123.87, 92.5) * mm});
            skArc(sketch, "E602", {"start": v(122.76, 87.78) * mm, "mid": v(122.52, 87.04) * mm, "end": v(122.76, 86.3) * mm});
            skLineSegment(sketch, "E603", {"start": v(125.05, 90.9) * mm, "end": v(122.76, 87.78) * mm});
            skArc(sketch, "E604", {"start": v(118.8, 91.68) * mm, "mid": v(119.43, 91.23) * mm, "end": v(120.21, 91.24) * mm});
            skLineSegment(sketch, "E605", {"start": v(123.87, 92.5) * mm, "end": v(120.21, 91.24) * mm});
            skArc(sketch, "E606", {"start": v(120.88, 96.38) * mm, "mid": v(120.26, 97.16) * mm, "end": v(119.62, 97.94) * mm});
            skArc(sketch, "E607", {"start": v(118.73, 93.16) * mm, "mid": v(118.52, 92.41) * mm, "end": v(118.8, 91.68) * mm});
            skLineSegment(sketch, "E608", {"start": v(120.88, 96.38) * mm, "end": v(118.73, 93.16) * mm});
            skArc(sketch, "E609", {"start": v(114.6, 96.88) * mm, "mid": v(115.25, 96.46) * mm, "end": v(116.03, 96.5) * mm});
            skLineSegment(sketch, "E610", {"start": v(119.62, 97.94) * mm, "end": v(116.03, 96.5) * mm});
            skArc(sketch, "E611", {"start": v(116.47, 101.67) * mm, "mid": v(115.8, 102.42) * mm, "end": v(115.14, 103.17) * mm});
            skArc(sketch, "E612", {"start": v(114.46, 98.36) * mm, "mid": v(114.29, 97.6) * mm, "end": v(114.6, 96.88) * mm});
            skLineSegment(sketch, "E613", {"start": v(116.47, 101.67) * mm, "end": v(114.46, 98.36) * mm});
            skArc(sketch, "E614", {"start": v(110.17, 101.9) * mm, "mid": v(110.84, 101.5) * mm, "end": v(111.62, 101.58) * mm});
            skLineSegment(sketch, "E615", {"start": v(115.14, 103.17) * mm, "end": v(111.62, 101.58) * mm});
            skArc(sketch, "E616", {"start": v(111.82, 106.75) * mm, "mid": v(111.13, 107.48) * mm, "end": v(110.43, 108.2) * mm});
            skArc(sketch, "E617", {"start": v(109.97, 103.36) * mm, "mid": v(109.83, 102.6) * mm, "end": v(110.17, 101.9) * mm});
            skLineSegment(sketch, "E618", {"start": v(111.82, 106.75) * mm, "end": v(109.97, 103.36) * mm});
            skArc(sketch, "E619", {"start": v(105.52, 106.7) * mm, "mid": v(106.2, 106.34) * mm, "end": v(106.98, 106.45) * mm});
            skLineSegment(sketch, "E620", {"start": v(110.43, 108.2) * mm, "end": v(106.98, 106.45) * mm});
            skArc(sketch, "E621", {"start": v(106.96, 111.63) * mm, "mid": v(106.23, 112.32) * mm, "end": v(105.5, 113) * mm});
            skArc(sketch, "E622", {"start": v(105.25, 108.16) * mm, "mid": v(105.15, 107.39) * mm, "end": v(105.52, 106.7) * mm});
            skLineSegment(sketch, "E623", {"start": v(106.96, 111.63) * mm, "end": v(105.25, 108.16) * mm});
            skArc(sketch, "E624", {"start": v(100.66, 111.3) * mm, "mid": v(101.37, 110.96) * mm, "end": v(102.13, 111.11) * mm});
            skLineSegment(sketch, "E625", {"start": v(105.5, 113) * mm, "end": v(102.13, 111.11) * mm});
            skArc(sketch, "E626", {"start": v(101.88, 116.28) * mm, "mid": v(101.12, 116.94) * mm, "end": v(100.36, 117.6) * mm});
            skArc(sketch, "E627", {"start": v(100.33, 112.74) * mm, "mid": v(100.26, 111.96) * mm, "end": v(100.66, 111.3) * mm});
            skLineSegment(sketch, "E628", {"start": v(101.88, 116.28) * mm, "end": v(100.33, 112.74) * mm});
            skArc(sketch, "E629", {"start": v(95.6, 115.67) * mm, "mid": v(96.32, 115.37) * mm, "end": v(97.08, 115.55) * mm});
            skLineSegment(sketch, "E630", {"start": v(100.36, 117.6) * mm, "end": v(97.08, 115.55) * mm});
            skArc(sketch, "E631", {"start": v(96.6, 120.7) * mm, "mid": v(95.81, 121.33) * mm, "end": v(95.03, 121.95) * mm});
            skArc(sketch, "E632", {"start": v(95.2, 117.1) * mm, "mid": v(95.17, 116.32) * mm, "end": v(95.6, 115.67) * mm});
            skLineSegment(sketch, "E633", {"start": v(96.6, 120.7) * mm, "end": v(95.2, 117.1) * mm});
            skArc(sketch, "E634", {"start": v(90.35, 119.81) * mm, "mid": v(91.09, 119.54) * mm, "end": v(91.84, 119.76) * mm});
            skLineSegment(sketch, "E635", {"start": v(95.03, 121.95) * mm, "end": v(91.84, 119.76) * mm});
            skArc(sketch, "E636", {"start": v(91.12, 124.9) * mm, "mid": v(90.31, 125.48) * mm, "end": v(89.5, 126.06) * mm});
            skArc(sketch, "E637", {"start": v(89.9, 121.22) * mm, "mid": v(89.9, 120.44) * mm, "end": v(90.35, 119.81) * mm});
            skLineSegment(sketch, "E638", {"start": v(91.12, 124.9) * mm, "end": v(89.9, 121.22) * mm});
            skArc(sketch, "E639", {"start": v(84.93, 123.72) * mm, "mid": v(85.67, 123.48) * mm, "end": v(86.4, 123.73) * mm});
            skLineSegment(sketch, "E640", {"start": v(89.5, 126.06) * mm, "end": v(86.4, 123.73) * mm});
            skArc(sketch, "E641", {"start": v(85.47, 128.83) * mm, "mid": v(84.63, 129.38) * mm, "end": v(83.8, 129.92) * mm});
            skArc(sketch, "E642", {"start": v(84.4, 125.1) * mm, "mid": v(84.44, 124.33) * mm, "end": v(84.93, 123.72) * mm});
            skLineSegment(sketch, "E643", {"start": v(85.47, 128.83) * mm, "end": v(84.4, 125.1) * mm});
            skArc(sketch, "E644", {"start": v(79.33, 127.38) * mm, "mid": v(80.09, 127.18) * mm, "end": v(80.81, 127.46) * mm});
            skLineSegment(sketch, "E645", {"start": v(83.8, 129.92) * mm, "end": v(80.81, 127.46) * mm});
            skArc(sketch, "E646", {"start": v(79.65, 132.5) * mm, "mid": v(78.79, 133.02) * mm, "end": v(77.92, 133.53) * mm});
            skArc(sketch, "E647", {"start": v(78.75, 128.74) * mm, "mid": v(78.82, 127.97) * mm, "end": v(79.33, 127.38) * mm});
            skLineSegment(sketch, "E648", {"start": v(79.65, 132.5) * mm, "end": v(78.75, 128.74) * mm});
            skArc(sketch, "E649", {"start": v(73.58, 130.79) * mm, "mid": v(74.34, 130.62) * mm, "end": v(75.05, 130.93) * mm});
            skLineSegment(sketch, "E650", {"start": v(77.92, 133.53) * mm, "end": v(75.05, 130.93) * mm});
            skArc(sketch, "E651", {"start": v(73.66, 135.92) * mm, "mid": v(72.78, 136.4) * mm, "end": v(71.9, 136.86) * mm});
            skArc(sketch, "E652", {"start": v(72.94, 132.12) * mm, "mid": v(73.04, 131.35) * mm, "end": v(73.58, 130.79) * mm});
            skLineSegment(sketch, "E653", {"start": v(73.66, 135.92) * mm, "end": v(72.94, 132.12) * mm});
            skArc(sketch, "E654", {"start": v(67.68, 133.93) * mm, "mid": v(68.45, 133.8) * mm, "end": v(69.15, 134.15) * mm});
            skLineSegment(sketch, "E655", {"start": v(71.9, 136.86) * mm, "end": v(69.15, 134.15) * mm});
            skArc(sketch, "E656", {"start": v(67.54, 139.07) * mm, "mid": v(66.63, 139.5) * mm, "end": v(65.73, 139.93) * mm});
            skArc(sketch, "E657", {"start": v(66.98, 135.24) * mm, "mid": v(67.12, 134.47) * mm, "end": v(67.68, 133.93) * mm});
            skLineSegment(sketch, "E658", {"start": v(67.54, 139.07) * mm, "end": v(66.98, 135.24) * mm});
            skArc(sketch, "E659", {"start": v(61.65, 136.82) * mm, "mid": v(62.42, 136.72) * mm, "end": v(63.1, 137.1) * mm});
            skLineSegment(sketch, "E660", {"start": v(65.73, 139.93) * mm, "end": v(63.1, 137.1) * mm});
            skArc(sketch, "E661", {"start": v(61.27, 141.94) * mm, "mid": v(60.35, 142.33) * mm, "end": v(59.43, 142.72) * mm});
            skArc(sketch, "E662", {"start": v(60.9, 138.1) * mm, "mid": v(61.06, 137.33) * mm, "end": v(61.65, 136.82) * mm});
            skLineSegment(sketch, "E663", {"start": v(61.27, 141.94) * mm, "end": v(60.9, 138.1) * mm});
            skArc(sketch, "E664", {"start": v(55.5, 139.43) * mm, "mid": v(56.27, 139.36) * mm, "end": v(56.93, 139.77) * mm});
            skLineSegment(sketch, "E665", {"start": v(59.43, 142.72) * mm, "end": v(56.93, 139.77) * mm});
            skArc(sketch, "E666", {"start": v(54.9, 144.53) * mm, "mid": v(53.95, 144.88) * mm, "end": v(53.01, 145.23) * mm});
            skArc(sketch, "E667", {"start": v(54.68, 140.67) * mm, "mid": v(54.88, 139.91) * mm, "end": v(55.5, 139.43) * mm});
            skLineSegment(sketch, "E668", {"start": v(54.9, 144.53) * mm, "end": v(54.68, 140.67) * mm});
            skArc(sketch, "E669", {"start": v(49.22, 141.76) * mm, "mid": v(50, 141.73) * mm, "end": v(50.65, 142.17) * mm});
            skLineSegment(sketch, "E670", {"start": v(53.01, 145.23) * mm, "end": v(50.65, 142.17) * mm});
            skArc(sketch, "E671", {"start": v(48.4, 146.83) * mm, "mid": v(47.45, 147.14) * mm, "end": v(46.5, 147.44) * mm});
            skArc(sketch, "E672", {"start": v(48.36, 142.96) * mm, "mid": v(48.6, 142.22) * mm, "end": v(49.22, 141.76) * mm});
            skLineSegment(sketch, "E673", {"start": v(48.4, 146.83) * mm, "end": v(48.36, 142.96) * mm});
            skArc(sketch, "E674", {"start": v(42.86, 143.81) * mm, "mid": v(43.64, 143.82) * mm, "end": v(44.27, 144.28) * mm});
            skLineSegment(sketch, "E675", {"start": v(46.5, 147.44) * mm, "end": v(44.27, 144.28) * mm});
            skArc(sketch, "E676", {"start": v(41.8, 148.84) * mm, "mid": v(40.84, 149.1) * mm, "end": v(39.88, 149.37) * mm});
            skArc(sketch, "E677", {"start": v(41.94, 144.97) * mm, "mid": v(42.21, 144.24) * mm, "end": v(42.86, 143.81) * mm});
            skLineSegment(sketch, "E678", {"start": v(41.8, 148.84) * mm, "end": v(41.94, 144.97) * mm});
            skArc(sketch, "E679", {"start": v(36.41, 145.58) * mm, "mid": v(37.2, 145.62) * mm, "end": v(37.8, 146.11) * mm});
            skLineSegment(sketch, "E680", {"start": v(39.88, 149.37) * mm, "end": v(37.8, 146.11) * mm});
            skArc(sketch, "E681", {"start": v(35.14, 150.55) * mm, "mid": v(34.16, 150.78) * mm, "end": v(33.18, 151) * mm});
            skArc(sketch, "E682", {"start": v(35.44, 146.7) * mm, "mid": v(35.74, 145.98) * mm, "end": v(36.41, 145.58) * mm});
            skLineSegment(sketch, "E683", {"start": v(35.14, 150.55) * mm, "end": v(35.44, 146.7) * mm});
            skArc(sketch, "E684", {"start": v(29.9, 147.06) * mm, "mid": v(30.67, 147.13) * mm, "end": v(31.25, 147.65) * mm});
            skLineSegment(sketch, "E685", {"start": v(33.18, 151) * mm, "end": v(31.25, 147.65) * mm});
            skArc(sketch, "E686", {"start": v(28.4, 151.97) * mm, "mid": v(27.41, 152.15) * mm, "end": v(26.43, 152.32) * mm});
            skArc(sketch, "E687", {"start": v(28.87, 148.13) * mm, "mid": v(29.2, 147.43) * mm, "end": v(29.9, 147.06) * mm});
            skLineSegment(sketch, "E688", {"start": v(28.4, 151.97) * mm, "end": v(28.87, 148.13) * mm});
            skArc(sketch, "E689", {"start": v(23.3, 148.24) * mm, "mid": v(24.08, 148.35) * mm, "end": v(24.64, 148.9) * mm});
            skLineSegment(sketch, "E690", {"start": v(26.43, 152.32) * mm, "end": v(24.64, 148.9) * mm});
            skArc(sketch, "E691", {"start": v(21.6, 153.08) * mm, "mid": v(20.6, 153.22) * mm, "end": v(19.61, 153.35) * mm});
            skArc(sketch, "E692", {"start": v(22.24, 149.27) * mm, "mid": v(22.6, 148.58) * mm, "end": v(23.3, 148.24) * mm});
            skLineSegment(sketch, "E693", {"start": v(21.6, 153.08) * mm, "end": v(22.24, 149.27) * mm});
            skArc(sketch, "E694", {"start": v(16.68, 149.13) * mm, "mid": v(17.45, 149.27) * mm, "end": v(17.98, 149.84) * mm});
            skLineSegment(sketch, "E695", {"start": v(19.61, 153.35) * mm, "end": v(17.98, 149.84) * mm});
            skArc(sketch, "E696", {"start": v(14.76, 153.9) * mm, "mid": v(13.76, 153.99) * mm, "end": v(12.76, 154.07) * mm});
            skArc(sketch, "E697", {"start": v(15.57, 150.11) * mm, "mid": v(15.97, 149.44) * mm, "end": v(16.68, 149.13) * mm});
            skLineSegment(sketch, "E698", {"start": v(14.76, 153.9) * mm, "end": v(15.57, 150.11) * mm});
            skArc(sketch, "E699", {"start": v(10.02, 149.73) * mm, "mid": v(10.78, 149.9) * mm, "end": v(11.3, 150.5) * mm});
            skLineSegment(sketch, "E700", {"start": v(12.76, 154.07) * mm, "end": v(11.3, 150.5) * mm});
            skArc(sketch, "E701", {"start": v(7.89, 154.4) * mm, "mid": v(6.89, 154.45) * mm, "end": v(5.89, 154.49) * mm});
            skArc(sketch, "E702", {"start": v(8.87, 150.66) * mm, "mid": v(9.3, 150) * mm, "end": v(10.02, 149.73) * mm});
            skLineSegment(sketch, "E703", {"start": v(7.89, 154.4) * mm, "end": v(8.87, 150.66) * mm});
            skArc(sketch, "E704", {"start": v(3.34, 150.03) * mm, "mid": v(4.1, 150.24) * mm, "end": v(4.57, 150.85) * mm});
            skLineSegment(sketch, "E705", {"start": v(5.89, 154.49) * mm, "end": v(4.57, 150.85) * mm});
            skSolve(sketch);
        }
        {
            var Q0;
            Q0 = qSketchRegion(id + "F0", true);
            extrude(context, id + "F1", {"entities" : qUnion([Q0]), "oppositeDirection" : true, "depth" : 8 * mm, "offsetDistance" : 25 * mm});
        }
    });
